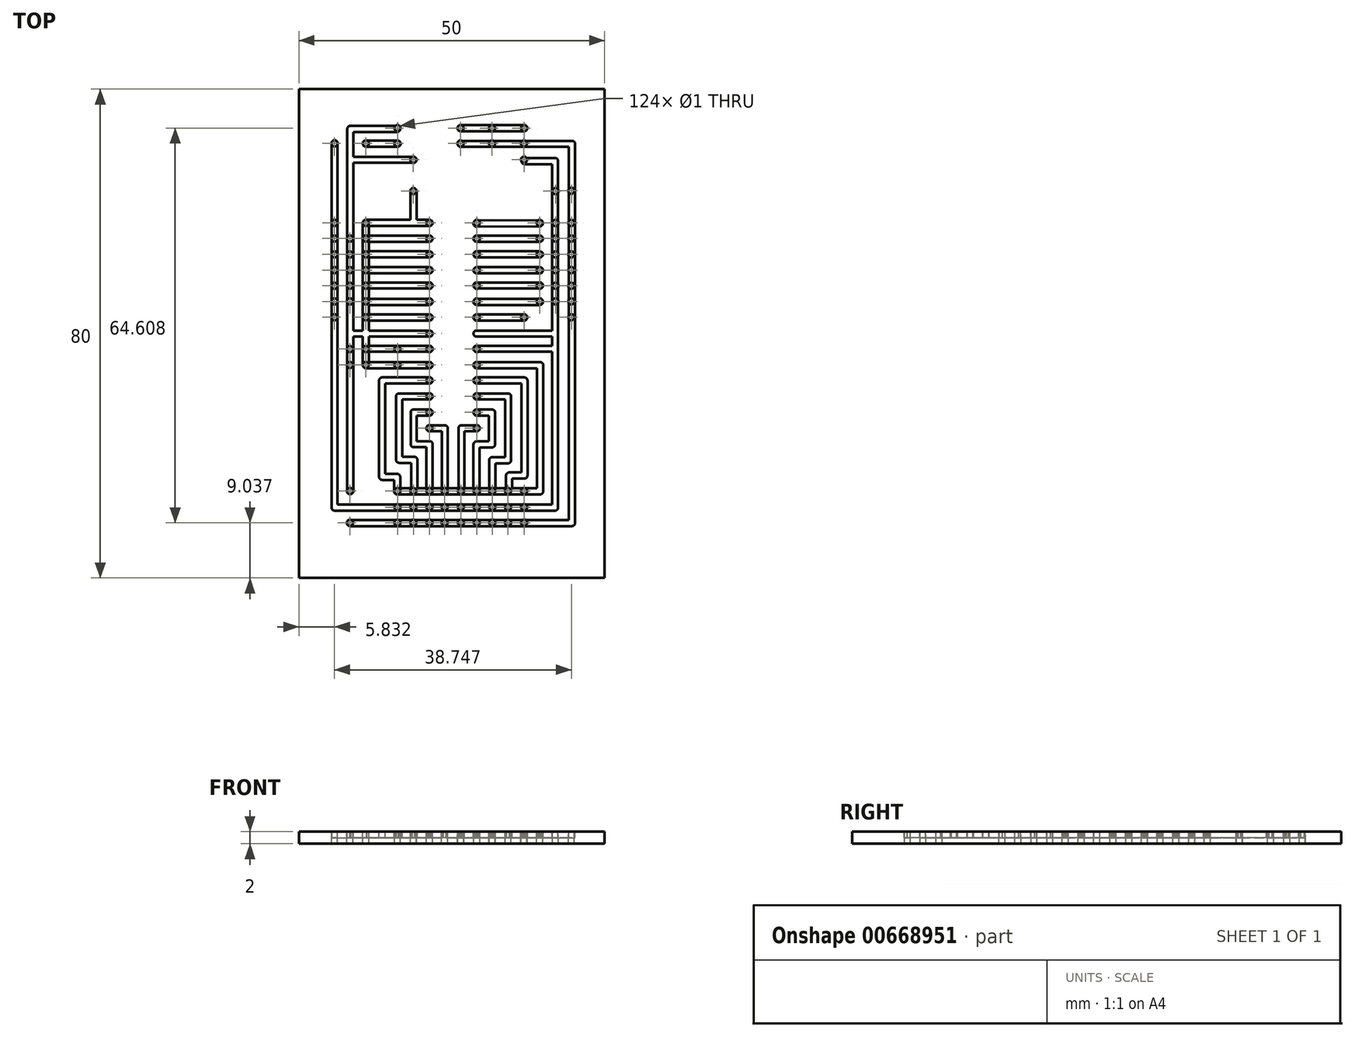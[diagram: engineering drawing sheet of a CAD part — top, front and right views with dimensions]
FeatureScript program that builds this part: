
annotation { "Feature Type Name" : "Feature", "Feature Type Description" : "" }
export const myFeature = defineFeature(function(context is Context, id is Id, definition is map)
    precondition{}
    {
        {
            var Q0;
            Q0=qCreatedBy(makeId("Top.planeOp"),FACE);
            var sketch = newSketch(context, id + "F0", { "sketchPlane" : qUnion([Q0])});
            skLineSegment(sketch, "E0.bottom", {"start": v(-25, 40) * mm, "end": v(25, 40) * mm});
            skLineSegment(sketch, "E0.top", {"start": v(-25, -40) * mm, "end": v(25, -40) * mm});
            skLineSegment(sketch, "E0.left", {"start": v(-25, 40) * mm, "end": v(-25, -40) * mm});
            skLineSegment(sketch, "E0.right", {"start": v(25, 40) * mm, "end": v(25, -40) * mm});
            skPoint(sketch, "E0.middle", {"position": v(0, 0) * mm});
            skPoint(sketch, "E1", {"position": v(0, 40) * mm});
            skLineSegment(sketch, "E2", {"start": v(0, 40) * mm, "end": v(0, 33.96) * mm});
            skPoint(sketch, "E3", {"position": v(-49.19, 30.9) * mm});
            skLineSegment(sketch, "E4", {"start": v(-19.68, -34.25) * mm, "end": v(20.32, -34.25) * mm});
            skSolve(sketch);
        }
        {
            var Q0;
            Q0=makeQuery(id+"F0.imprint","IMPRINT",FACE,{"disambiguationData":[TD([[makeQuery(id+"F0.imprint","IMPRINT",EDGE,{"derivedFrom":sQuery(id+"F0.wireOp",EDGE,"E0.top")}),1.0]])]});
            var sketch = newSketch(context, id + "F1", { "sketchPlane" : qUnion([Q0])});
            skLineSegment(sketch, "E5", {"start": v(-19.15, 31.14) * mm, "end": v(-19.15, -28.48) * mm});
            skLineSegment(sketch, "E6", {"start": v(-19.15, -28.48) * mm, "end": v(16.9, -28.48) * mm});
            skLineSegment(sketch, "E7", {"start": v(16.9, -28.48) * mm, "end": v(16.9, 28.23) * mm});
            skLineSegment(sketch, "E8", {"start": v(16.9, 28.23) * mm, "end": v(11.93, 28.23) * mm});
            skLineSegment(sketch, "E9", {"start": v(4.07, 5.19) * mm, "end": v(14.43, 5.19) * mm});
            skLineSegment(sketch, "E10", {"start": v(4.07, 7.87) * mm, "end": v(14.43, 7.87) * mm});
            skLineSegment(sketch, "E11", {"start": v(4.07, 10.35) * mm, "end": v(14.43, 10.35) * mm});
            skLineSegment(sketch, "E12", {"start": v(4.07, 12.96) * mm, "end": v(14.43, 12.96) * mm});
            skLineSegment(sketch, "E13", {"start": v(4.07, 15.53) * mm, "end": v(14.43, 15.53) * mm});
            skLineSegment(sketch, "E14", {"start": v(4.07, 17.98) * mm, "end": v(14.43, 18.06) * mm});
            skLineSegment(sketch, "E15", {"start": v(4.07, 2.63) * mm, "end": v(11.86, 2.63) * mm});
            skLineSegment(sketch, "E16", {"start": v(4.07, 0) * mm, "end": v(16.9, 0) * mm});
            skLineSegment(sketch, "E17", {"start": v(4.07, -2.48) * mm, "end": v(16.9, -2.48) * mm});
            skLineSegment(sketch, "E18", {"start": v(4.07, -5.17) * mm, "end": v(14.47, -5.17) * mm});
            skLineSegment(sketch, "E19", {"start": v(14.47, -5.17) * mm, "end": v(14.47, -25.82) * mm});
            skLineSegment(sketch, "E20", {"start": v(14.47, -25.82) * mm, "end": v(11.84, -25.82) * mm});
            skLineSegment(sketch, "E21", {"start": v(11.84, -25.82) * mm, "end": v(-8.92, -25.82) * mm});
            skLineSegment(sketch, "E22", {"start": v(-8.92, -25.82) * mm, "end": v(-8.92, -23.45) * mm});
            skLineSegment(sketch, "E23", {"start": v(-8.92, -23.45) * mm, "end": v(-11.37, -23.45) * mm});
            skLineSegment(sketch, "E24", {"start": v(-11.37, -23.45) * mm, "end": v(-11.37, -7.68) * mm});
            skLineSegment(sketch, "E25", {"start": v(-11.37, -7.68) * mm, "end": v(-3.63, -7.68) * mm});
            skLineSegment(sketch, "E26", {"start": v(-3.63, 18.1) * mm, "end": v(-14.04, 18.1) * mm});
            skLineSegment(sketch, "E27", {"start": v(-14.04, 18.1) * mm, "end": v(-14.04, -5.18) * mm});
            skLineSegment(sketch, "E28", {"start": v(-3.63, 15.53) * mm, "end": v(-14.04, 15.53) * mm});
            skLineSegment(sketch, "E29", {"start": v(-3.63, 12.96) * mm, "end": v(-14.04, 12.96) * mm});
            skLineSegment(sketch, "E30", {"start": v(-3.63, 10.35) * mm, "end": v(-14.04, 10.35) * mm});
            skLineSegment(sketch, "E31", {"start": v(-3.63, 7.87) * mm, "end": v(-14.04, 7.87) * mm});
            skLineSegment(sketch, "E32", {"start": v(-3.63, 5.19) * mm, "end": v(-14.04, 5.19) * mm});
            skLineSegment(sketch, "E33", {"start": v(-3.63, 2.63) * mm, "end": v(-14.04, 2.63) * mm});
            skLineSegment(sketch, "E34", {"start": v(-3.63, -2.48) * mm, "end": v(-14.04, -2.48) * mm});
            skLineSegment(sketch, "E35", {"start": v(-3.63, -5.17) * mm, "end": v(-14.04, -5.18) * mm});
            skLineSegment(sketch, "E36", {"start": v(4.07, -7.68) * mm, "end": v(11.9, -7.68) * mm});
            skLineSegment(sketch, "E37", {"start": v(11.9, -7.68) * mm, "end": v(11.9, -23.23) * mm});
            skLineSegment(sketch, "E38", {"start": v(11.9, -23.23) * mm, "end": v(9.4, -23.23) * mm});
            skLineSegment(sketch, "E39", {"start": v(9.4, -23.23) * mm, "end": v(9.4, -25.82) * mm});
            skLineSegment(sketch, "E40", {"start": v(4.07, -10.3) * mm, "end": v(9.22, -10.3) * mm});
            skLineSegment(sketch, "E41", {"start": v(9.22, -10.3) * mm, "end": v(9.22, -20.73) * mm});
            skLineSegment(sketch, "E42", {"start": v(9.22, -20.73) * mm, "end": v(6.63, -20.73) * mm});
            skLineSegment(sketch, "E43", {"start": v(6.63, -20.73) * mm, "end": v(6.63, -25.82) * mm});
            skLineSegment(sketch, "E44", {"start": v(4.07, -12.92) * mm, "end": v(6.59, -12.92) * mm});
            skLineSegment(sketch, "E45", {"start": v(6.59, -12.92) * mm, "end": v(6.59, -18.14) * mm});
            skLineSegment(sketch, "E46", {"start": v(6.59, -18.14) * mm, "end": v(4.07, -18.14) * mm});
            skLineSegment(sketch, "E47", {"start": v(4.07, -18.14) * mm, "end": v(4.07, -25.82) * mm});
            skLineSegment(sketch, "E48", {"start": v(1.6, -15.5) * mm, "end": v(1.6, -25.82) * mm});
            skLineSegment(sketch, "E49", {"start": v(-1.13, -25.82) * mm, "end": v(-1.13, -15.5) * mm});
            skLineSegment(sketch, "E50", {"start": v(-3.63, -25.82) * mm, "end": v(-3.63, -18.1) * mm});
            skLineSegment(sketch, "E51", {"start": v(-3.63, -18.1) * mm, "end": v(-6.21, -18.1) * mm});
            skLineSegment(sketch, "E52", {"start": v(-3.63, -10.3) * mm, "end": v(-8.6, -10.3) * mm});
            skLineSegment(sketch, "E53", {"start": v(-8.6, -10.3) * mm, "end": v(-8.6, -20.65) * mm});
            skLineSegment(sketch, "E54", {"start": v(-8.6, -20.65) * mm, "end": v(-6.11, -20.65) * mm});
            skLineSegment(sketch, "E55", {"start": v(-6.11, -20.65) * mm, "end": v(-6.11, -25.82) * mm});
            skLineSegment(sketch, "E56", {"start": v(-3.63, -12.92) * mm, "end": v(-6.21, -12.92) * mm});
            skLineSegment(sketch, "E57", {"start": v(-6.21, -12.92) * mm, "end": v(-6.21, -18.1) * mm});
            skLineSegment(sketch, "E58", {"start": v(-6.25, 23.32) * mm, "end": v(-6.25, 18.1) * mm});
            skLineSegment(sketch, "E59", {"start": v(-3.63, 0) * mm, "end": v(-16.57, 0) * mm});
            skLineSegment(sketch, "E60", {"start": v(-16.57, 0) * mm, "end": v(-16.57, 33.5) * mm});
            skLineSegment(sketch, "E61", {"start": v(-16.57, 33.5) * mm, "end": v(-8.92, 33.5) * mm});
            skLineSegment(sketch, "E62", {"start": v(-14.04, 31.08) * mm, "end": v(-8.84, 31.08) * mm});
            skLineSegment(sketch, "E63", {"start": v(-6.24, 28.44) * mm, "end": v(-16.57, 28.44) * mm});
            skLineSegment(sketch, "E64", {"start": v(1.48, 33.63) * mm, "end": v(11.88, 33.63) * mm});
            skLineSegment(sketch, "E65", {"start": v(1.48, 31.05) * mm, "end": v(19.67, 31.05) * mm});
            skLineSegment(sketch, "E66", {"start": v(19.67, 31.05) * mm, "end": v(19.67, -31) * mm});
            skLineSegment(sketch, "E67", {"start": v(19.67, -31) * mm, "end": v(-16.64, -31) * mm});
            skLineSegment(sketch, "E68", {"start": v(-16.57, 0) * mm, "end": v(-16.57, -25.78) * mm});
            skLineSegment(sketch, "E69", {"start": v(-3.64, -15.5) * mm, "end": v(-1.13, -15.5) * mm});
            skLineSegment(sketch, "E70", {"start": v(1.6, -15.5) * mm, "end": v(4.07, -15.5) * mm});
            skArc(sketch, "E71.0.startCap", {"start": v(-3.63, 16.03) * mm, "mid": v(-3.13, 15.53) * mm, "end": v(-3.63, 15.03) * mm});
            skArc(sketch, "E71.0.endCap", {"start": v(-14.04, 15.03) * mm, "mid": v(-14.54, 15.53) * mm, "end": v(-14.04, 16.03) * mm});
            skLineSegment(sketch, "E71.0.left", {"start": v(-3.63, 15.03) * mm, "end": v(-14.04, 15.03) * mm});
            skLineSegment(sketch, "E71.0.right", {"start": v(-3.63, 16.03) * mm, "end": v(-14.04, 16.03) * mm});
            skArc(sketch, "E71.1.startCap", {"start": v(11.4, -7.68) * mm, "mid": v(11.9, -7.18) * mm, "end": v(12.4, -7.68) * mm});
            skArc(sketch, "E71.1.endCap", {"start": v(12.4, -23.23) * mm, "mid": v(11.9, -23.73) * mm, "end": v(11.4, -23.23) * mm});
            skLineSegment(sketch, "E71.1.left", {"start": v(12.4, -7.68) * mm, "end": v(12.4, -23.23) * mm});
            skLineSegment(sketch, "E71.1.right", {"start": v(11.4, -7.68) * mm, "end": v(11.4, -23.23) * mm});
            skArc(sketch, "E71.2.endCap", {"start": v(-16.07, -25.78) * mm, "mid": v(-16.57, -26.28) * mm, "end": v(-17.07, -25.78) * mm});
            skLineSegment(sketch, "E71.2.left", {"start": v(-16.07, 0) * mm, "end": v(-16.07, -25.78) * mm});
            skLineSegment(sketch, "E71.2.right", {"start": v(-17.07, 0) * mm, "end": v(-17.07, -25.78) * mm});
            skArc(sketch, "E71.3.startCap", {"start": v(4.07, 7.37) * mm, "mid": v(3.57, 7.87) * mm, "end": v(4.07, 8.37) * mm});
            skArc(sketch, "E71.3.endCap", {"start": v(14.43, 8.37) * mm, "mid": v(14.93, 7.87) * mm, "end": v(14.43, 7.37) * mm});
            skLineSegment(sketch, "E71.3.left", {"start": v(4.07, 8.37) * mm, "end": v(14.43, 8.37) * mm});
            skLineSegment(sketch, "E71.3.right", {"start": v(4.07, 7.37) * mm, "end": v(14.43, 7.37) * mm});
            skArc(sketch, "E71.4.startCap", {"start": v(-8.92, -22.95) * mm, "mid": v(-8.42, -23.45) * mm, "end": v(-8.92, -23.95) * mm});
            skArc(sketch, "E71.4.endCap", {"start": v(-11.37, -23.95) * mm, "mid": v(-11.87, -23.45) * mm, "end": v(-11.37, -22.95) * mm});
            skLineSegment(sketch, "E71.4.left", {"start": v(-8.92, -23.95) * mm, "end": v(-11.37, -23.95) * mm});
            skLineSegment(sketch, "E71.4.right", {"start": v(-8.92, -22.95) * mm, "end": v(-11.37, -22.95) * mm});
            skArc(sketch, "E71.5.startCap", {"start": v(11.84, -25.32) * mm, "mid": v(12.34, -25.82) * mm, "end": v(11.84, -26.32) * mm});
            skArc(sketch, "E71.5.endCap", {"start": v(-8.92, -26.32) * mm, "mid": v(-9.42, -25.82) * mm, "end": v(-8.92, -25.32) * mm});
            skLineSegment(sketch, "E71.5.left", {"start": v(11.84, -26.32) * mm, "end": v(-8.92, -26.32) * mm});
            skLineSegment(sketch, "E71.5.right", {"start": v(11.84, -25.32) * mm, "end": v(-8.92, -25.32) * mm});
            skArc(sketch, "E71.6.startCap", {"start": v(11.9, -22.73) * mm, "mid": v(12.4, -23.23) * mm, "end": v(11.9, -23.73) * mm});
            skArc(sketch, "E71.6.endCap", {"start": v(9.4, -23.73) * mm, "mid": v(8.9, -23.23) * mm, "end": v(9.4, -22.73) * mm});
            skLineSegment(sketch, "E71.6.left", {"start": v(11.9, -23.73) * mm, "end": v(9.4, -23.73) * mm});
            skLineSegment(sketch, "E71.6.right", {"start": v(11.9, -22.73) * mm, "end": v(9.4, -22.73) * mm});
            skArc(sketch, "E71.7.startCap", {"start": v(-8.6, -21.15) * mm, "mid": v(-9.1, -20.65) * mm, "end": v(-8.6, -20.15) * mm});
            skArc(sketch, "E71.7.endCap", {"start": v(-6.11, -20.15) * mm, "mid": v(-5.61, -20.65) * mm, "end": v(-6.11, -21.15) * mm});
            skLineSegment(sketch, "E71.7.left", {"start": v(-8.6, -20.15) * mm, "end": v(-6.11, -20.15) * mm});
            skLineSegment(sketch, "E71.7.right", {"start": v(-8.6, -21.15) * mm, "end": v(-6.11, -21.15) * mm});
            skArc(sketch, "E71.8.startCap", {"start": v(19.67, -30.5) * mm, "mid": v(20.17, -31) * mm, "end": v(19.67, -31.5) * mm});
            skArc(sketch, "E71.8.endCap", {"start": v(-16.64, -31.5) * mm, "mid": v(-17.14, -31) * mm, "end": v(-16.64, -30.5) * mm});
            skLineSegment(sketch, "E71.8.left", {"start": v(19.67, -31.5) * mm, "end": v(-16.64, -31.5) * mm});
            skLineSegment(sketch, "E71.8.right", {"start": v(19.67, -30.5) * mm, "end": v(-16.64, -30.5) * mm});
            skArc(sketch, "E71.9.startCap", {"start": v(-3.64, -16) * mm, "mid": v(-4.14, -15.5) * mm, "end": v(-3.64, -15) * mm});
            skArc(sketch, "E71.9.endCap", {"start": v(-1.13, -15) * mm, "mid": v(-0.63, -15.5) * mm, "end": v(-1.13, -16) * mm});
            skLineSegment(sketch, "E71.9.left", {"start": v(-3.64, -15) * mm, "end": v(-1.13, -15) * mm});
            skLineSegment(sketch, "E71.9.right", {"start": v(-3.64, -16) * mm, "end": v(-1.13, -16) * mm});
            skArc(sketch, "E71.10.startCap", {"start": v(6.13, -20.73) * mm, "mid": v(6.63, -20.23) * mm, "end": v(7.13, -20.73) * mm});
            skArc(sketch, "E71.10.endCap", {"start": v(7.13, -25.82) * mm, "mid": v(6.63, -26.32) * mm, "end": v(6.13, -25.82) * mm});
            skLineSegment(sketch, "E71.10.left", {"start": v(7.13, -20.73) * mm, "end": v(7.13, -25.82) * mm});
            skLineSegment(sketch, "E71.10.right", {"start": v(6.13, -20.73) * mm, "end": v(6.13, -25.82) * mm});
            skArc(sketch, "E71.11.startCap", {"start": v(14.47, -25.32) * mm, "mid": v(14.97, -25.82) * mm, "end": v(14.47, -26.32) * mm});
            skArc(sketch, "E71.11.endCap", {"start": v(11.84, -26.32) * mm, "mid": v(11.34, -25.82) * mm, "end": v(11.84, -25.32) * mm});
            skLineSegment(sketch, "E71.11.left", {"start": v(14.47, -26.32) * mm, "end": v(11.84, -26.32) * mm});
            skLineSegment(sketch, "E71.11.right", {"start": v(14.47, -25.32) * mm, "end": v(11.84, -25.32) * mm});
            skArc(sketch, "E71.12.startCap", {"start": v(4.07, -8.18) * mm, "mid": v(3.57, -7.68) * mm, "end": v(4.07, -7.18) * mm});
            skArc(sketch, "E71.12.endCap", {"start": v(11.9, -7.18) * mm, "mid": v(12.4, -7.68) * mm, "end": v(11.9, -8.18) * mm});
            skLineSegment(sketch, "E71.12.left", {"start": v(4.07, -7.18) * mm, "end": v(11.9, -7.18) * mm});
            skLineSegment(sketch, "E71.12.right", {"start": v(4.07, -8.18) * mm, "end": v(11.9, -8.18) * mm});
            skArc(sketch, "E71.13.startCap", {"start": v(4.07, 2.13) * mm, "mid": v(3.57, 2.63) * mm, "end": v(4.07, 3.13) * mm});
            skArc(sketch, "E71.13.endCap", {"start": v(11.86, 3.13) * mm, "mid": v(12.36, 2.63) * mm, "end": v(11.86, 2.13) * mm});
            skLineSegment(sketch, "E71.13.left", {"start": v(4.07, 3.13) * mm, "end": v(11.86, 3.13) * mm});
            skLineSegment(sketch, "E71.13.right", {"start": v(4.07, 2.13) * mm, "end": v(11.86, 2.13) * mm});
            skArc(sketch, "E71.14.startCap", {"start": v(-14.54, 18.1) * mm, "mid": v(-14.04, 18.6) * mm, "end": v(-13.54, 18.1) * mm});
            skArc(sketch, "E71.14.endCap", {"start": v(-13.54, -5.18) * mm, "mid": v(-14.04, -5.68) * mm, "end": v(-14.54, -5.18) * mm});
            skLineSegment(sketch, "E71.14.left", {"start": v(-13.54, 18.1) * mm, "end": v(-13.54, -5.18) * mm});
            skLineSegment(sketch, "E71.14.right", {"start": v(-14.54, 18.1) * mm, "end": v(-14.54, -5.18) * mm});
            skArc(sketch, "E71.15.startCap", {"start": v(-3.63, 0.5) * mm, "mid": v(-3.13, 0) * mm, "end": v(-3.63, -0.5) * mm});
            skArc(sketch, "E71.15.endCap", {"start": v(-16.57, -0.5) * mm, "mid": v(-17.07, 0) * mm, "end": v(-16.57, 0.5) * mm});
            skLineSegment(sketch, "E71.15.left", {"start": v(-3.63, -0.5) * mm, "end": v(-16.57, -0.5) * mm});
            skLineSegment(sketch, "E71.15.right", {"start": v(-3.63, 0.5) * mm, "end": v(-16.57, 0.5) * mm});
            skArc(sketch, "E71.16.startCap", {"start": v(-3.63, -9.8) * mm, "mid": v(-3.13, -10.3) * mm, "end": v(-3.63, -10.8) * mm});
            skArc(sketch, "E71.16.endCap", {"start": v(-8.6, -10.8) * mm, "mid": v(-9.1, -10.3) * mm, "end": v(-8.6, -9.8) * mm});
            skLineSegment(sketch, "E71.16.left", {"start": v(-3.63, -10.8) * mm, "end": v(-8.6, -10.8) * mm});
            skLineSegment(sketch, "E71.16.right", {"start": v(-3.63, -9.8) * mm, "end": v(-8.6, -9.8) * mm});
            skArc(sketch, "E71.17.startCap", {"start": v(4.07, -0.5) * mm, "mid": v(3.57, 0) * mm, "end": v(4.07, 0.5) * mm});
            skArc(sketch, "E71.17.endCap", {"start": v(16.9, 0.5) * mm, "mid": v(17.4, 0) * mm, "end": v(16.9, -0.5) * mm});
            skLineSegment(sketch, "E71.17.left", {"start": v(4.07, 0.5) * mm, "end": v(16.9, 0.5) * mm});
            skLineSegment(sketch, "E71.17.right", {"start": v(4.07, -0.5) * mm, "end": v(16.9, -0.5) * mm});
            skArc(sketch, "E71.18.startCap", {"start": v(4.07, -2.98) * mm, "mid": v(3.57, -2.48) * mm, "end": v(4.07, -1.98) * mm});
            skArc(sketch, "E71.18.endCap", {"start": v(16.9, -1.98) * mm, "mid": v(17.4, -2.48) * mm, "end": v(16.9, -2.98) * mm});
            skLineSegment(sketch, "E71.18.left", {"start": v(4.07, -1.98) * mm, "end": v(16.9, -1.98) * mm});
            skLineSegment(sketch, "E71.18.right", {"start": v(4.07, -2.98) * mm, "end": v(16.9, -2.98) * mm});
            skArc(sketch, "E71.19.startCap", {"start": v(-8.42, -25.82) * mm, "mid": v(-8.92, -26.32) * mm, "end": v(-9.42, -25.82) * mm});
            skArc(sketch, "E71.19.endCap", {"start": v(-9.42, -23.45) * mm, "mid": v(-8.92, -22.95) * mm, "end": v(-8.42, -23.45) * mm});
            skLineSegment(sketch, "E71.19.left", {"start": v(-9.42, -25.82) * mm, "end": v(-9.42, -23.45) * mm});
            skLineSegment(sketch, "E71.19.right", {"start": v(-8.42, -25.82) * mm, "end": v(-8.42, -23.45) * mm});
            skArc(sketch, "E71.20.startCap", {"start": v(4.07, 9.85) * mm, "mid": v(3.57, 10.35) * mm, "end": v(4.07, 10.85) * mm});
            skArc(sketch, "E71.20.endCap", {"start": v(14.43, 10.85) * mm, "mid": v(14.93, 10.35) * mm, "end": v(14.43, 9.85) * mm});
            skLineSegment(sketch, "E71.20.left", {"start": v(4.07, 10.85) * mm, "end": v(14.43, 10.85) * mm});
            skLineSegment(sketch, "E71.20.right", {"start": v(4.07, 9.85) * mm, "end": v(14.43, 9.85) * mm});
            skArc(sketch, "E71.21.startCap", {"start": v(1.6, -16) * mm, "mid": v(1.1, -15.5) * mm, "end": v(1.6, -15) * mm});
            skArc(sketch, "E71.21.endCap", {"start": v(4.07, -15) * mm, "mid": v(4.57, -15.5) * mm, "end": v(4.07, -16) * mm});
            skLineSegment(sketch, "E71.21.left", {"start": v(1.6, -15) * mm, "end": v(4.07, -15) * mm});
            skLineSegment(sketch, "E71.21.right", {"start": v(1.6, -16) * mm, "end": v(4.07, -16) * mm});
            skArc(sketch, "E71.22.startCap", {"start": v(4.07, 12.46) * mm, "mid": v(3.57, 12.96) * mm, "end": v(4.07, 13.46) * mm});
            skArc(sketch, "E71.22.endCap", {"start": v(14.43, 13.46) * mm, "mid": v(14.93, 12.96) * mm, "end": v(14.43, 12.46) * mm});
            skLineSegment(sketch, "E71.22.left", {"start": v(4.07, 13.46) * mm, "end": v(14.43, 13.46) * mm});
            skLineSegment(sketch, "E71.22.right", {"start": v(4.07, 12.46) * mm, "end": v(14.43, 12.46) * mm});
            skArc(sketch, "E71.23.startCap", {"start": v(-6.75, 23.32) * mm, "mid": v(-6.25, 23.82) * mm, "end": v(-5.75, 23.32) * mm});
            skArc(sketch, "E71.23.endCap", {"start": v(-5.75, 18.1) * mm, "mid": v(-6.25, 17.6) * mm, "end": v(-6.75, 18.1) * mm});
            skLineSegment(sketch, "E71.23.left", {"start": v(-5.75, 23.32) * mm, "end": v(-5.75, 18.1) * mm});
            skLineSegment(sketch, "E71.23.right", {"start": v(-6.75, 23.32) * mm, "end": v(-6.75, 18.1) * mm});
            skArc(sketch, "E71.24.startCap", {"start": v(-3.63, 18.6) * mm, "mid": v(-3.13, 18.1) * mm, "end": v(-3.63, 17.6) * mm});
            skArc(sketch, "E71.24.endCap", {"start": v(-14.04, 17.6) * mm, "mid": v(-14.54, 18.1) * mm, "end": v(-14.04, 18.6) * mm});
            skLineSegment(sketch, "E71.24.left", {"start": v(-3.63, 17.6) * mm, "end": v(-14.04, 17.6) * mm});
            skLineSegment(sketch, "E71.24.right", {"start": v(-3.63, 18.6) * mm, "end": v(-14.04, 18.6) * mm});
            skArc(sketch, "E71.25.startCap", {"start": v(-19.65, 31.14) * mm, "mid": v(-19.15, 31.64) * mm, "end": v(-18.65, 31.14) * mm});
            skArc(sketch, "E71.25.endCap", {"start": v(-18.65, -28.48) * mm, "mid": v(-19.15, -28.98) * mm, "end": v(-19.65, -28.48) * mm});
            skLineSegment(sketch, "E71.25.left", {"start": v(-18.65, 31.14) * mm, "end": v(-18.65, -28.48) * mm});
            skLineSegment(sketch, "E71.25.right", {"start": v(-19.65, 31.14) * mm, "end": v(-19.65, -28.48) * mm});
            skArc(sketch, "E71.26.startCap", {"start": v(1.1, -15.5) * mm, "mid": v(1.6, -15) * mm, "end": v(2.1, -15.5) * mm});
            skArc(sketch, "E71.26.endCap", {"start": v(2.1, -25.82) * mm, "mid": v(1.6, -26.32) * mm, "end": v(1.1, -25.82) * mm});
            skLineSegment(sketch, "E71.26.left", {"start": v(2.1, -15.5) * mm, "end": v(2.1, -25.82) * mm});
            skLineSegment(sketch, "E71.26.right", {"start": v(1.1, -15.5) * mm, "end": v(1.1, -25.82) * mm});
            skArc(sketch, "E71.27.startCap", {"start": v(-3.63, 5.69) * mm, "mid": v(-3.13, 5.19) * mm, "end": v(-3.63, 4.69) * mm});
            skArc(sketch, "E71.27.endCap", {"start": v(-14.04, 4.69) * mm, "mid": v(-14.54, 5.19) * mm, "end": v(-14.04, 5.69) * mm});
            skLineSegment(sketch, "E71.27.left", {"start": v(-3.63, 4.69) * mm, "end": v(-14.04, 4.69) * mm});
            skLineSegment(sketch, "E71.27.right", {"start": v(-3.63, 5.69) * mm, "end": v(-14.04, 5.69) * mm});
            skArc(sketch, "E71.28.startCap", {"start": v(4.07, 17.48) * mm, "mid": v(3.57, 17.98) * mm, "end": v(4.06, 18.48) * mm});
            skArc(sketch, "E71.28.endCap", {"start": v(14.42, 18.56) * mm, "mid": v(14.93, 18.06) * mm, "end": v(14.43, 17.56) * mm});
            skLineSegment(sketch, "E71.28.left", {"start": v(4.06, 18.48) * mm, "end": v(14.42, 18.56) * mm});
            skLineSegment(sketch, "E71.28.right", {"start": v(4.07, 17.48) * mm, "end": v(14.43, 17.56) * mm});
            skArc(sketch, "E71.29.startCap", {"start": v(4.07, 15.03) * mm, "mid": v(3.57, 15.53) * mm, "end": v(4.07, 16.03) * mm});
            skArc(sketch, "E71.29.endCap", {"start": v(14.43, 16.03) * mm, "mid": v(14.93, 15.53) * mm, "end": v(14.43, 15.03) * mm});
            skLineSegment(sketch, "E71.29.left", {"start": v(4.07, 16.03) * mm, "end": v(14.43, 16.03) * mm});
            skLineSegment(sketch, "E71.29.right", {"start": v(4.07, 15.03) * mm, "end": v(14.43, 15.03) * mm});
            skArc(sketch, "E71.30.startCap", {"start": v(-6.61, -20.65) * mm, "mid": v(-6.11, -20.15) * mm, "end": v(-5.61, -20.65) * mm});
            skArc(sketch, "E71.30.endCap", {"start": v(-5.61, -25.82) * mm, "mid": v(-6.11, -26.32) * mm, "end": v(-6.61, -25.82) * mm});
            skLineSegment(sketch, "E71.30.left", {"start": v(-5.61, -20.65) * mm, "end": v(-5.61, -25.82) * mm});
            skLineSegment(sketch, "E71.30.right", {"start": v(-6.61, -20.65) * mm, "end": v(-6.61, -25.82) * mm});
            skArc(sketch, "E71.31.startCap", {"start": v(1.48, 30.55) * mm, "mid": v(0.98, 31.05) * mm, "end": v(1.48, 31.55) * mm});
            skArc(sketch, "E71.31.endCap", {"start": v(19.67, 31.55) * mm, "mid": v(20.17, 31.05) * mm, "end": v(19.67, 30.55) * mm});
            skLineSegment(sketch, "E71.31.left", {"start": v(1.48, 31.55) * mm, "end": v(19.67, 31.55) * mm});
            skLineSegment(sketch, "E71.31.right", {"start": v(1.48, 30.55) * mm, "end": v(19.67, 30.55) * mm});
            skArc(sketch, "E71.32.startCap", {"start": v(-6.71, -12.92) * mm, "mid": v(-6.21, -12.42) * mm, "end": v(-5.71, -12.92) * mm});
            skArc(sketch, "E71.32.endCap", {"start": v(-5.71, -18.1) * mm, "mid": v(-6.21, -18.6) * mm, "end": v(-6.71, -18.1) * mm});
            skLineSegment(sketch, "E71.32.left", {"start": v(-5.71, -12.92) * mm, "end": v(-5.71, -18.1) * mm});
            skLineSegment(sketch, "E71.32.right", {"start": v(-6.71, -12.92) * mm, "end": v(-6.71, -18.1) * mm});
            skArc(sketch, "E71.33.startCap", {"start": v(-11.37, -8.18) * mm, "mid": v(-11.87, -7.68) * mm, "end": v(-11.37, -7.18) * mm});
            skArc(sketch, "E71.33.endCap", {"start": v(-3.63, -7.18) * mm, "mid": v(-3.13, -7.68) * mm, "end": v(-3.63, -8.18) * mm});
            skLineSegment(sketch, "E71.33.left", {"start": v(-11.37, -7.18) * mm, "end": v(-3.63, -7.18) * mm});
            skLineSegment(sketch, "E71.33.right", {"start": v(-11.37, -8.18) * mm, "end": v(-3.63, -8.18) * mm});
            skArc(sketch, "E71.34.startCap", {"start": v(17.4, -28.48) * mm, "mid": v(16.9, -28.98) * mm, "end": v(16.4, -28.48) * mm});
            skArc(sketch, "E71.34.endCap", {"start": v(16.4, 28.23) * mm, "mid": v(16.9, 28.73) * mm, "end": v(17.4, 28.23) * mm});
            skLineSegment(sketch, "E71.34.left", {"start": v(16.4, -28.48) * mm, "end": v(16.4, 28.23) * mm});
            skLineSegment(sketch, "E71.34.right", {"start": v(17.4, -28.48) * mm, "end": v(17.4, 28.23) * mm});
            skArc(sketch, "E71.35.startCap", {"start": v(-3.63, 3.13) * mm, "mid": v(-3.13, 2.63) * mm, "end": v(-3.63, 2.13) * mm});
            skArc(sketch, "E71.35.endCap", {"start": v(-14.04, 2.13) * mm, "mid": v(-14.54, 2.63) * mm, "end": v(-14.04, 3.13) * mm});
            skLineSegment(sketch, "E71.35.left", {"start": v(-3.63, 2.13) * mm, "end": v(-14.04, 2.13) * mm});
            skLineSegment(sketch, "E71.35.right", {"start": v(-3.63, 3.13) * mm, "end": v(-14.04, 3.13) * mm});
            skArc(sketch, "E71.36.startCap", {"start": v(-16.57, 33) * mm, "mid": v(-17.07, 33.5) * mm, "end": v(-16.57, 34) * mm});
            skArc(sketch, "E71.36.endCap", {"start": v(-8.92, 34) * mm, "mid": v(-8.42, 33.5) * mm, "end": v(-8.92, 33) * mm});
            skLineSegment(sketch, "E71.36.left", {"start": v(-16.57, 34) * mm, "end": v(-8.92, 34) * mm});
            skLineSegment(sketch, "E71.36.right", {"start": v(-16.57, 33) * mm, "end": v(-8.92, 33) * mm});
            skArc(sketch, "E71.37.startCap", {"start": v(6.09, -12.92) * mm, "mid": v(6.59, -12.42) * mm, "end": v(7.09, -12.92) * mm});
            skArc(sketch, "E71.37.endCap", {"start": v(7.09, -18.14) * mm, "mid": v(6.59, -18.64) * mm, "end": v(6.09, -18.14) * mm});
            skLineSegment(sketch, "E71.37.left", {"start": v(7.09, -12.92) * mm, "end": v(7.09, -18.14) * mm});
            skLineSegment(sketch, "E71.37.right", {"start": v(6.09, -12.92) * mm, "end": v(6.09, -18.14) * mm});
            skArc(sketch, "E71.38.startCap", {"start": v(-9.1, -10.3) * mm, "mid": v(-8.6, -9.8) * mm, "end": v(-8.1, -10.3) * mm});
            skArc(sketch, "E71.38.endCap", {"start": v(-8.1, -20.65) * mm, "mid": v(-8.6, -21.15) * mm, "end": v(-9.1, -20.65) * mm});
            skLineSegment(sketch, "E71.38.left", {"start": v(-8.1, -10.3) * mm, "end": v(-8.1, -20.65) * mm});
            skLineSegment(sketch, "E71.38.right", {"start": v(-9.1, -10.3) * mm, "end": v(-9.1, -20.65) * mm});
            skArc(sketch, "E71.39.startCap", {"start": v(-3.63, 13.46) * mm, "mid": v(-3.13, 12.96) * mm, "end": v(-3.63, 12.46) * mm});
            skArc(sketch, "E71.39.endCap", {"start": v(-14.04, 12.46) * mm, "mid": v(-14.54, 12.96) * mm, "end": v(-14.04, 13.46) * mm});
            skLineSegment(sketch, "E71.39.left", {"start": v(-3.63, 12.46) * mm, "end": v(-14.04, 12.46) * mm});
            skLineSegment(sketch, "E71.39.right", {"start": v(-3.63, 13.46) * mm, "end": v(-14.04, 13.46) * mm});
            skArc(sketch, "E71.40.startCap", {"start": v(4.07, 4.69) * mm, "mid": v(3.57, 5.19) * mm, "end": v(4.07, 5.69) * mm});
            skArc(sketch, "E71.40.endCap", {"start": v(14.43, 5.69) * mm, "mid": v(14.93, 5.19) * mm, "end": v(14.43, 4.69) * mm});
            skLineSegment(sketch, "E71.40.left", {"start": v(4.07, 5.69) * mm, "end": v(14.43, 5.69) * mm});
            skLineSegment(sketch, "E71.40.right", {"start": v(4.07, 4.69) * mm, "end": v(14.43, 4.69) * mm});
            skArc(sketch, "E71.41.startCap", {"start": v(16.9, 28.73) * mm, "mid": v(17.4, 28.23) * mm, "end": v(16.9, 27.73) * mm});
            skArc(sketch, "E71.41.endCap", {"start": v(11.93, 27.73) * mm, "mid": v(11.43, 28.23) * mm, "end": v(11.93, 28.73) * mm});
            skLineSegment(sketch, "E71.41.left", {"start": v(16.9, 27.73) * mm, "end": v(11.93, 27.73) * mm});
            skLineSegment(sketch, "E71.41.right", {"start": v(16.9, 28.73) * mm, "end": v(11.93, 28.73) * mm});
            skArc(sketch, "E71.42.startCap", {"start": v(-3.63, 10.85) * mm, "mid": v(-3.13, 10.35) * mm, "end": v(-3.63, 9.85) * mm});
            skArc(sketch, "E71.42.endCap", {"start": v(-14.04, 9.85) * mm, "mid": v(-14.54, 10.35) * mm, "end": v(-14.04, 10.85) * mm});
            skLineSegment(sketch, "E71.42.left", {"start": v(-3.63, 9.85) * mm, "end": v(-14.04, 9.85) * mm});
            skLineSegment(sketch, "E71.42.right", {"start": v(-3.63, 10.85) * mm, "end": v(-14.04, 10.85) * mm});
            skArc(sketch, "E71.43.startCap", {"start": v(19.17, 31.05) * mm, "mid": v(19.67, 31.55) * mm, "end": v(20.17, 31.05) * mm});
            skArc(sketch, "E71.43.endCap", {"start": v(20.17, -31) * mm, "mid": v(19.67, -31.5) * mm, "end": v(19.17, -31) * mm});
            skLineSegment(sketch, "E71.43.left", {"start": v(20.17, 31.05) * mm, "end": v(20.17, -31) * mm});
            skLineSegment(sketch, "E71.43.right", {"start": v(19.17, 31.05) * mm, "end": v(19.17, -31) * mm});
            skArc(sketch, "E71.44.startCap", {"start": v(1.48, 33.13) * mm, "mid": v(0.98, 33.63) * mm, "end": v(1.48, 34.13) * mm});
            skArc(sketch, "E71.44.endCap", {"start": v(11.88, 34.13) * mm, "mid": v(12.38, 33.63) * mm, "end": v(11.88, 33.13) * mm});
            skLineSegment(sketch, "E71.44.left", {"start": v(1.48, 34.13) * mm, "end": v(11.88, 34.13) * mm});
            skLineSegment(sketch, "E71.44.right", {"start": v(1.48, 33.13) * mm, "end": v(11.88, 33.13) * mm});
            skArc(sketch, "E71.45.startCap", {"start": v(-19.15, -28.98) * mm, "mid": v(-19.65, -28.48) * mm, "end": v(-19.15, -27.98) * mm});
            skArc(sketch, "E71.45.endCap", {"start": v(16.9, -27.98) * mm, "mid": v(17.4, -28.48) * mm, "end": v(16.9, -28.98) * mm});
            skLineSegment(sketch, "E71.45.left", {"start": v(-19.15, -27.98) * mm, "end": v(16.9, -27.98) * mm});
            skLineSegment(sketch, "E71.45.right", {"start": v(-19.15, -28.98) * mm, "end": v(16.9, -28.98) * mm});
            skArc(sketch, "E71.46.startCap", {"start": v(8.9, -23.23) * mm, "mid": v(9.4, -22.73) * mm, "end": v(9.9, -23.23) * mm});
            skArc(sketch, "E71.46.endCap", {"start": v(9.9, -25.82) * mm, "mid": v(9.4, -26.32) * mm, "end": v(8.9, -25.82) * mm});
            skLineSegment(sketch, "E71.46.left", {"start": v(9.9, -23.23) * mm, "end": v(9.9, -25.82) * mm});
            skLineSegment(sketch, "E71.46.right", {"start": v(8.9, -23.23) * mm, "end": v(8.9, -25.82) * mm});
            skArc(sketch, "E71.47.startCap", {"start": v(-3.13, -25.82) * mm, "mid": v(-3.63, -26.32) * mm, "end": v(-4.13, -25.82) * mm});
            skArc(sketch, "E71.47.endCap", {"start": v(-4.13, -18.1) * mm, "mid": v(-3.63, -17.6) * mm, "end": v(-3.13, -18.1) * mm});
            skLineSegment(sketch, "E71.47.left", {"start": v(-4.13, -25.82) * mm, "end": v(-4.13, -18.1) * mm});
            skLineSegment(sketch, "E71.47.right", {"start": v(-3.13, -25.82) * mm, "end": v(-3.13, -18.1) * mm});
            skArc(sketch, "E71.48.startCap", {"start": v(-3.63, -1.98) * mm, "mid": v(-3.13, -2.48) * mm, "end": v(-3.63, -2.98) * mm});
            skArc(sketch, "E71.48.endCap", {"start": v(-14.04, -2.98) * mm, "mid": v(-14.54, -2.48) * mm, "end": v(-14.04, -1.98) * mm});
            skLineSegment(sketch, "E71.48.left", {"start": v(-3.63, -2.98) * mm, "end": v(-14.04, -2.98) * mm});
            skLineSegment(sketch, "E71.48.right", {"start": v(-3.63, -1.98) * mm, "end": v(-14.04, -1.98) * mm});
            skArc(sketch, "E71.49.startCap", {"start": v(8.72, -10.3) * mm, "mid": v(9.22, -9.8) * mm, "end": v(9.72, -10.3) * mm});
            skArc(sketch, "E71.49.endCap", {"start": v(9.72, -20.73) * mm, "mid": v(9.22, -21.23) * mm, "end": v(8.72, -20.73) * mm});
            skLineSegment(sketch, "E71.49.left", {"start": v(9.72, -10.3) * mm, "end": v(9.72, -20.73) * mm});
            skLineSegment(sketch, "E71.49.right", {"start": v(8.72, -10.3) * mm, "end": v(8.72, -20.73) * mm});
            skArc(sketch, "E71.50.endCap", {"start": v(-17.07, 33.5) * mm, "mid": v(-16.57, 34) * mm, "end": v(-16.07, 33.5) * mm});
            skLineSegment(sketch, "E71.50.left", {"start": v(-17.07, 0) * mm, "end": v(-17.07, 33.5) * mm});
            skLineSegment(sketch, "E71.50.right", {"start": v(-16.07, 0) * mm, "end": v(-16.07, 33.5) * mm});
            skArc(sketch, "E71.51.startCap", {"start": v(4.07, -13.42) * mm, "mid": v(3.57, -12.92) * mm, "end": v(4.07, -12.42) * mm});
            skArc(sketch, "E71.51.endCap", {"start": v(6.59, -12.42) * mm, "mid": v(7.09, -12.92) * mm, "end": v(6.59, -13.42) * mm});
            skLineSegment(sketch, "E71.51.left", {"start": v(4.07, -12.42) * mm, "end": v(6.59, -12.42) * mm});
            skLineSegment(sketch, "E71.51.right", {"start": v(4.07, -13.42) * mm, "end": v(6.59, -13.42) * mm});
            skArc(sketch, "E71.52.startCap", {"start": v(-3.63, -4.67) * mm, "mid": v(-3.13, -5.17) * mm, "end": v(-3.63, -5.67) * mm});
            skArc(sketch, "E71.52.endCap", {"start": v(-14.04, -5.68) * mm, "mid": v(-14.54, -5.18) * mm, "end": v(-14.04, -4.68) * mm});
            skLineSegment(sketch, "E71.52.left", {"start": v(-3.63, -5.67) * mm, "end": v(-14.04, -5.68) * mm});
            skLineSegment(sketch, "E71.52.right", {"start": v(-3.63, -4.67) * mm, "end": v(-14.04, -4.68) * mm});
            skArc(sketch, "E71.53.startCap", {"start": v(-3.63, -17.6) * mm, "mid": v(-3.13, -18.1) * mm, "end": v(-3.63, -18.6) * mm});
            skArc(sketch, "E71.53.endCap", {"start": v(-6.21, -18.6) * mm, "mid": v(-6.71, -18.1) * mm, "end": v(-6.21, -17.6) * mm});
            skLineSegment(sketch, "E71.53.left", {"start": v(-3.63, -18.6) * mm, "end": v(-6.21, -18.6) * mm});
            skLineSegment(sketch, "E71.53.right", {"start": v(-3.63, -17.6) * mm, "end": v(-6.21, -17.6) * mm});
            skArc(sketch, "E71.54.startCap", {"start": v(9.22, -20.23) * mm, "mid": v(9.72, -20.73) * mm, "end": v(9.22, -21.23) * mm});
            skArc(sketch, "E71.54.endCap", {"start": v(6.63, -21.23) * mm, "mid": v(6.13, -20.73) * mm, "end": v(6.63, -20.23) * mm});
            skLineSegment(sketch, "E71.54.left", {"start": v(9.22, -21.23) * mm, "end": v(6.63, -21.23) * mm});
            skLineSegment(sketch, "E71.54.right", {"start": v(9.22, -20.23) * mm, "end": v(6.63, -20.23) * mm});
            skArc(sketch, "E71.55.startCap", {"start": v(13.97, -5.17) * mm, "mid": v(14.47, -4.67) * mm, "end": v(14.97, -5.17) * mm});
            skArc(sketch, "E71.55.endCap", {"start": v(14.97, -25.82) * mm, "mid": v(14.47, -26.32) * mm, "end": v(13.97, -25.82) * mm});
            skLineSegment(sketch, "E71.55.left", {"start": v(14.97, -5.17) * mm, "end": v(14.97, -25.82) * mm});
            skLineSegment(sketch, "E71.55.right", {"start": v(13.97, -5.17) * mm, "end": v(13.97, -25.82) * mm});
            skArc(sketch, "E71.56.startCap", {"start": v(-0.63, -25.82) * mm, "mid": v(-1.13, -26.32) * mm, "end": v(-1.63, -25.82) * mm});
            skArc(sketch, "E71.56.endCap", {"start": v(-1.63, -15.5) * mm, "mid": v(-1.13, -15) * mm, "end": v(-0.63, -15.5) * mm});
            skLineSegment(sketch, "E71.56.left", {"start": v(-1.63, -25.82) * mm, "end": v(-1.63, -15.5) * mm});
            skLineSegment(sketch, "E71.56.right", {"start": v(-0.63, -25.82) * mm, "end": v(-0.63, -15.5) * mm});
            skArc(sketch, "E71.57.startCap", {"start": v(-14.04, 30.58) * mm, "mid": v(-14.54, 31.08) * mm, "end": v(-14.04, 31.58) * mm});
            skArc(sketch, "E71.57.endCap", {"start": v(-8.84, 31.58) * mm, "mid": v(-8.34, 31.08) * mm, "end": v(-8.84, 30.58) * mm});
            skLineSegment(sketch, "E71.57.left", {"start": v(-14.04, 31.58) * mm, "end": v(-8.84, 31.58) * mm});
            skLineSegment(sketch, "E71.57.right", {"start": v(-14.04, 30.58) * mm, "end": v(-8.84, 30.58) * mm});
            skArc(sketch, "E71.58.startCap", {"start": v(6.59, -17.64) * mm, "mid": v(7.09, -18.14) * mm, "end": v(6.59, -18.64) * mm});
            skArc(sketch, "E71.58.endCap", {"start": v(4.07, -18.64) * mm, "mid": v(3.57, -18.14) * mm, "end": v(4.07, -17.64) * mm});
            skLineSegment(sketch, "E71.58.left", {"start": v(6.59, -18.64) * mm, "end": v(4.07, -18.64) * mm});
            skLineSegment(sketch, "E71.58.right", {"start": v(6.59, -17.64) * mm, "end": v(4.07, -17.64) * mm});
            skArc(sketch, "E71.59.startCap", {"start": v(4.07, -5.67) * mm, "mid": v(3.57, -5.17) * mm, "end": v(4.07, -4.67) * mm});
            skArc(sketch, "E71.59.endCap", {"start": v(14.47, -4.67) * mm, "mid": v(14.97, -5.17) * mm, "end": v(14.47, -5.67) * mm});
            skLineSegment(sketch, "E71.59.left", {"start": v(4.07, -4.67) * mm, "end": v(14.47, -4.67) * mm});
            skLineSegment(sketch, "E71.59.right", {"start": v(4.07, -5.67) * mm, "end": v(14.47, -5.67) * mm});
            skArc(sketch, "E71.60.startCap", {"start": v(-3.63, 8.37) * mm, "mid": v(-3.13, 7.87) * mm, "end": v(-3.63, 7.37) * mm});
            skArc(sketch, "E71.60.endCap", {"start": v(-14.04, 7.37) * mm, "mid": v(-14.54, 7.87) * mm, "end": v(-14.04, 8.37) * mm});
            skLineSegment(sketch, "E71.60.left", {"start": v(-3.63, 7.37) * mm, "end": v(-14.04, 7.37) * mm});
            skLineSegment(sketch, "E71.60.right", {"start": v(-3.63, 8.37) * mm, "end": v(-14.04, 8.37) * mm});
            skArc(sketch, "E71.61.startCap", {"start": v(-6.24, 28.94) * mm, "mid": v(-5.74, 28.44) * mm, "end": v(-6.24, 27.94) * mm});
            skArc(sketch, "E71.61.endCap", {"start": v(-16.57, 27.94) * mm, "mid": v(-17.07, 28.44) * mm, "end": v(-16.57, 28.94) * mm});
            skLineSegment(sketch, "E71.61.left", {"start": v(-6.24, 27.94) * mm, "end": v(-16.57, 27.94) * mm});
            skLineSegment(sketch, "E71.61.right", {"start": v(-6.24, 28.94) * mm, "end": v(-16.57, 28.94) * mm});
            skArc(sketch, "E71.62.startCap", {"start": v(3.57, -18.14) * mm, "mid": v(4.07, -17.64) * mm, "end": v(4.57, -18.14) * mm});
            skArc(sketch, "E71.62.endCap", {"start": v(4.57, -25.82) * mm, "mid": v(4.07, -26.32) * mm, "end": v(3.57, -25.82) * mm});
            skLineSegment(sketch, "E71.62.left", {"start": v(4.57, -18.14) * mm, "end": v(4.57, -25.82) * mm});
            skLineSegment(sketch, "E71.62.right", {"start": v(3.57, -18.14) * mm, "end": v(3.57, -25.82) * mm});
            skArc(sketch, "E71.63.startCap", {"start": v(-3.63, -12.42) * mm, "mid": v(-3.13, -12.92) * mm, "end": v(-3.63, -13.42) * mm});
            skArc(sketch, "E71.63.endCap", {"start": v(-6.21, -13.42) * mm, "mid": v(-6.71, -12.92) * mm, "end": v(-6.21, -12.42) * mm});
            skLineSegment(sketch, "E71.63.left", {"start": v(-3.63, -13.42) * mm, "end": v(-6.21, -13.42) * mm});
            skLineSegment(sketch, "E71.63.right", {"start": v(-3.63, -12.42) * mm, "end": v(-6.21, -12.42) * mm});
            skArc(sketch, "E71.64.startCap", {"start": v(4.07, -10.8) * mm, "mid": v(3.57, -10.3) * mm, "end": v(4.07, -9.8) * mm});
            skArc(sketch, "E71.64.endCap", {"start": v(9.22, -9.8) * mm, "mid": v(9.72, -10.3) * mm, "end": v(9.22, -10.8) * mm});
            skLineSegment(sketch, "E71.64.left", {"start": v(4.07, -9.8) * mm, "end": v(9.22, -9.8) * mm});
            skLineSegment(sketch, "E71.64.right", {"start": v(4.07, -10.8) * mm, "end": v(9.22, -10.8) * mm});
            skArc(sketch, "E71.65.startCap", {"start": v(-10.87, -23.45) * mm, "mid": v(-11.37, -23.95) * mm, "end": v(-11.87, -23.45) * mm});
            skArc(sketch, "E71.65.endCap", {"start": v(-11.87, -7.68) * mm, "mid": v(-11.37, -7.18) * mm, "end": v(-10.87, -7.68) * mm});
            skLineSegment(sketch, "E71.65.left", {"start": v(-11.87, -23.45) * mm, "end": v(-11.87, -7.68) * mm});
            skLineSegment(sketch, "E71.65.right", {"start": v(-10.87, -23.45) * mm, "end": v(-10.87, -7.68) * mm});
            skSolve(sketch);
        }
        {
            var Q0;
            Q0=makeQuery(id+"F0.imprint","IMPRINT",FACE,{"disambiguationData":[TD([[makeQuery(id+"F0.imprint","IMPRINT",EDGE,{"derivedFrom":sQuery(id+"F0.wireOp",EDGE,"E0.top")}),1.0]])]});
            var sketch = newSketch(context, id + "F2", { "sketchPlane" : qUnion([Q0])});
            skPoint(sketch, "E72", {"position": v(-19.17, 31.12) * mm});
            skPoint(sketch, "E73", {"position": v(-19.17, 18.12) * mm});
            skPoint(sketch, "E74", {"position": v(-19.17, 15.55) * mm});
            skPoint(sketch, "E75", {"position": v(-19.17, 12.96) * mm});
            skPoint(sketch, "E76", {"position": v(-19.17, 10.38) * mm});
            skPoint(sketch, "E77", {"position": v(-19.17, 7.83) * mm});
            skPoint(sketch, "E78", {"position": v(-19.17, 5.26) * mm});
            skPoint(sketch, "E79", {"position": v(-19.17, 2.67) * mm});
            skPoint(sketch, "E80", {"position": v(-16.64, -30.96) * mm});
            skPoint(sketch, "E81", {"position": v(-16.64, -25.77) * mm});
            skPoint(sketch, "E82", {"position": v(-16.64, -5.14) * mm});
            skPoint(sketch, "E83", {"position": v(-16.64, -2.53) * mm});
            skPoint(sketch, "E84", {"position": v(-16.64, 5.26) * mm});
            skPoint(sketch, "E85", {"position": v(-16.64, 7.83) * mm});
            skPoint(sketch, "E86", {"position": v(-16.64, 10.38) * mm});
            skPoint(sketch, "E87", {"position": v(-16.64, 12.96) * mm});
            skPoint(sketch, "E88", {"position": v(-16.64, 15.55) * mm});
            skPoint(sketch, "E89", {"position": v(-14.04, 31.12) * mm});
            skPoint(sketch, "E90", {"position": v(-14.04, 18.12) * mm});
            skPoint(sketch, "E91", {"position": v(-8.87, 31.12) * mm});
            skPoint(sketch, "E92", {"position": v(-8.87, 33.65) * mm});
            skPoint(sketch, "E93", {"position": v(-14.04, 15.55) * mm});
            skPoint(sketch, "E94", {"position": v(-14.04, 12.96) * mm});
            skPoint(sketch, "E95", {"position": v(-14.04, 10.38) * mm});
            skPoint(sketch, "E96", {"position": v(-3.63, 18.12) * mm});
            skPoint(sketch, "E97", {"position": v(-3.63, 15.55) * mm});
            skPoint(sketch, "E98", {"position": v(-3.63, 12.96) * mm});
            skPoint(sketch, "E99", {"position": v(-3.63, 10.38) * mm});
            skPoint(sketch, "E100", {"position": v(-14.04, 7.83) * mm});
            skPoint(sketch, "E101", {"position": v(-3.63, 7.83) * mm});
            skPoint(sketch, "E102", {"position": v(-14.04, 5.26) * mm});
            skPoint(sketch, "E103", {"position": v(-3.63, 5.26) * mm});
            skPoint(sketch, "E104", {"position": v(-14.04, 2.67) * mm});
            skPoint(sketch, "E105", {"position": v(-3.63, 2.67) * mm});
            skPoint(sketch, "E106", {"position": v(-3.63, 0) * mm});
            skPoint(sketch, "E107", {"position": v(-14.04, -2.53) * mm});
            skPoint(sketch, "E108", {"position": v(-8.87, -2.53) * mm});
            skPoint(sketch, "E109", {"position": v(-3.63, -2.53) * mm});
            skPoint(sketch, "E110", {"position": v(-14.04, -5.14) * mm});
            skPoint(sketch, "E111", {"position": v(-8.87, -5.14) * mm});
            skPoint(sketch, "E112", {"position": v(-3.63, -5.14) * mm});
            skPoint(sketch, "E113", {"position": v(-3.63, -7.65) * mm});
            skPoint(sketch, "E114", {"position": v(-3.63, -10.26) * mm});
            skPoint(sketch, "E115", {"position": v(-3.63, -12.9) * mm});
            skPoint(sketch, "E116", {"position": v(-3.63, -15.47) * mm});
            skPoint(sketch, "E117", {"position": v(-8.87, -25.77) * mm});
            skPoint(sketch, "E118", {"position": v(-8.87, -28.41) * mm});
            skPoint(sketch, "E119", {"position": v(-8.87, -30.95) * mm});
            skPoint(sketch, "E120", {"position": v(-6.26, -25.77) * mm});
            skPoint(sketch, "E121", {"position": v(-3.63, -25.77) * mm});
            skPoint(sketch, "E122", {"position": v(-1.15, -25.77) * mm});
            skPoint(sketch, "E123", {"position": v(1.51, -25.77) * mm});
            skPoint(sketch, "E124", {"position": v(4.11, -25.77) * mm});
            skPoint(sketch, "E125", {"position": v(6.65, -25.77) * mm});
            skPoint(sketch, "E126", {"position": v(9.22, -25.77) * mm});
            skPoint(sketch, "E127", {"position": v(11.85, -25.77) * mm});
            skPoint(sketch, "E128", {"position": v(-6.26, -28.41) * mm});
            skPoint(sketch, "E129", {"position": v(-3.63, -28.41) * mm});
            skPoint(sketch, "E130", {"position": v(-1.15, -28.41) * mm});
            skPoint(sketch, "E131", {"position": v(1.51, -28.41) * mm});
            skPoint(sketch, "E132", {"position": v(4.11, -28.41) * mm});
            skPoint(sketch, "E133", {"position": v(6.65, -28.41) * mm});
            skPoint(sketch, "E134", {"position": v(9.22, -28.41) * mm});
            skPoint(sketch, "E135", {"position": v(11.85, -28.41) * mm});
            skPoint(sketch, "E136", {"position": v(11.85, -30.95) * mm});
            skPoint(sketch, "E137", {"position": v(9.22, -30.95) * mm});
            skPoint(sketch, "E138", {"position": v(6.65, -30.95) * mm});
            skPoint(sketch, "E139", {"position": v(4.11, -30.95) * mm});
            skPoint(sketch, "E140", {"position": v(1.51, -30.95) * mm});
            skPoint(sketch, "E141", {"position": v(-1.15, -30.95) * mm});
            skPoint(sketch, "E142", {"position": v(-3.63, -30.95) * mm});
            skPoint(sketch, "E143", {"position": v(-6.26, -30.95) * mm});
            skPoint(sketch, "E144", {"position": v(4.11, -15.47) * mm});
            skPoint(sketch, "E145", {"position": v(4.11, -12.9) * mm});
            skPoint(sketch, "E146", {"position": v(4.11, -10.26) * mm});
            skPoint(sketch, "E147", {"position": v(4.11, -7.65) * mm});
            skPoint(sketch, "E148", {"position": v(4.11, -5.14) * mm});
            skPoint(sketch, "E149", {"position": v(4.11, -2.53) * mm});
            skPoint(sketch, "E150", {"position": v(4.11, 0) * mm});
            skPoint(sketch, "E151", {"position": v(4.11, 10.38) * mm});
            skPoint(sketch, "E152", {"position": v(4.11, 7.83) * mm});
            skPoint(sketch, "E153", {"position": v(4.11, 5.26) * mm});
            skPoint(sketch, "E154", {"position": v(4.11, 2.67) * mm});
            skPoint(sketch, "E155", {"position": v(4.11, 12.96) * mm});
            skPoint(sketch, "E156", {"position": v(4.11, 15.55) * mm});
            skPoint(sketch, "E157", {"position": v(4.11, 18.12) * mm});
            skPoint(sketch, "E158", {"position": v(14.4, 18.12) * mm});
            skPoint(sketch, "E159", {"position": v(14.4, 15.55) * mm});
            skPoint(sketch, "E160", {"position": v(14.4, 12.96) * mm});
            skPoint(sketch, "E161", {"position": v(14.4, 10.38) * mm});
            skPoint(sketch, "E162", {"position": v(14.4, 7.83) * mm});
            skPoint(sketch, "E163", {"position": v(14.4, 5.26) * mm});
            skPoint(sketch, "E164", {"position": v(11.85, 2.67) * mm});
            skPoint(sketch, "E165", {"position": v(16.97, 5.26) * mm});
            skPoint(sketch, "E166", {"position": v(19.58, 5.26) * mm});
            skPoint(sketch, "E167", {"position": v(19.58, 7.83) * mm});
            skPoint(sketch, "E168", {"position": v(19.58, 10.38) * mm});
            skPoint(sketch, "E169", {"position": v(19.58, 12.96) * mm});
            skPoint(sketch, "E170", {"position": v(19.58, 15.55) * mm});
            skPoint(sketch, "E171", {"position": v(19.58, 18.12) * mm});
            skPoint(sketch, "E172", {"position": v(16.97, 18.12) * mm});
            skPoint(sketch, "E173", {"position": v(16.97, 15.55) * mm});
            skPoint(sketch, "E174", {"position": v(16.97, 12.96) * mm});
            skPoint(sketch, "E175", {"position": v(16.97, 10.38) * mm});
            skPoint(sketch, "E176", {"position": v(16.97, 7.83) * mm});
            skPoint(sketch, "E177", {"position": v(16.97, 23.33) * mm});
            skPoint(sketch, "E178", {"position": v(19.58, 23.38) * mm});
            skPoint(sketch, "E179", {"position": v(11.84, 28.46) * mm});
            skPoint(sketch, "E180", {"position": v(11.81, 31.12) * mm});
            skPoint(sketch, "E181", {"position": v(11.87, 33.62) * mm});
            skPoint(sketch, "E182", {"position": v(6.6, 33.62) * mm});
            skPoint(sketch, "E183", {"position": v(6.6, 31.12) * mm});
            skPoint(sketch, "E184", {"position": v(1.44, 31.12) * mm});
            skPoint(sketch, "E185", {"position": v(1.44, 33.62) * mm});
            skPoint(sketch, "E186", {"position": v(-6.27, 28.46) * mm});
            skPoint(sketch, "E187", {"position": v(-6.27, 23.33) * mm});
            skPoint(sketch, "E188", {"position": v(19.58, 2.67) * mm});
            skSolve(sketch);
        }
        {
            var Q0;
            Q0=makeQuery(id+"F0.imprint","IMPRINT",FACE,{"disambiguationData":[TD([[makeQuery(id+"F0.imprint","IMPRINT",EDGE,{"derivedFrom":sQuery(id+"F0.wireOp",EDGE,"E0.top")}),1.0]])]});
            extrude(context, id + "F3", {"entities" : qUnion([Q0]), "oppositeDirection" : true, "depth" : 2 * mm, "offsetDistance" : 25 * mm});
        }
        {
            var Q0;
            Q0 = qSketchRegion(id + "F1", true);
            extrude(context, id + "F4", {"entities" : qUnion([Q0]), "operationType" : NewBodyOperationType.REMOVE, "oppositeDirection" : true, "depth" : 1 * mm, "offsetDistance" : 25 * mm});
        }
        {
            var Q0;
            Q0 = qSketchRegion(id + "F1", true);
            extrude(context, id + "F5", {"entities" : qUnion([Q0]), "oppositeDirection" : true, "depth" : 1 * mm, "offsetDistance" : 25 * mm});
        }
        {
            var Q0;
            Q0=sQuery(id+"F2.wireOp",VERTEX,"E118");
            var Q1;
            Q1=sQuery(id+"F2.wireOp",VERTEX,"E72");
            var Q2;
            Q2=sQuery(id+"F2.wireOp",VERTEX,"E85");
            var Q3;
            Q3=sQuery(id+"F2.wireOp",VERTEX,"E83");
            var Q4;
            Q4=sQuery(id+"F2.wireOp",VERTEX,"E84");
            var Q5;
            Q5=sQuery(id+"F2.wireOp",VERTEX,"E82");
            var Q6;
            Q6=sQuery(id+"F2.wireOp",VERTEX,"E81");
            var Q7;
            Q7=sQuery(id+"F2.wireOp",VERTEX,"E77");
            var Q8;
            Q8=sQuery(id+"F2.wireOp",VERTEX,"E73");
            var Q9;
            Q9=sQuery(id+"F2.wireOp",VERTEX,"E86");
            var Q10;
            Q10=sQuery(id+"F2.wireOp",VERTEX,"E87");
            var Q11;
            Q11=sQuery(id+"F2.wireOp",VERTEX,"E80");
            var Q12;
            Q12=sQuery(id+"F2.wireOp",VERTEX,"E76");
            var Q13;
            Q13=sQuery(id+"F2.wireOp",VERTEX,"E78");
            var Q14;
            Q14=sQuery(id+"F2.wireOp",VERTEX,"E79");
            var Q15;
            Q15=sQuery(id+"F2.wireOp",VERTEX,"E74");
            var Q16;
            Q16=sQuery(id+"F2.wireOp",VERTEX,"E75");
            var Q17;
            Q17=sQuery(id+"F2.wireOp",VERTEX,"E111");
            var Q18;
            Q18=sQuery(id+"F2.wireOp",VERTEX,"E95");
            var Q19;
            Q19=sQuery(id+"F2.wireOp",VERTEX,"E112");
            var Q20;
            Q20=sQuery(id+"F2.wireOp",VERTEX,"E143");
            var Q21;
            Q21=sQuery(id+"F2.wireOp",VERTEX,"E142");
            var Q22;
            Q22=sQuery(id+"F2.wireOp",VERTEX,"E110");
            var Q23;
            Q23=sQuery(id+"F2.wireOp",VERTEX,"E94");
            var Q24;
            Q24=sQuery(id+"F2.wireOp",VERTEX,"E100");
            var Q25;
            Q25=sQuery(id+"F2.wireOp",VERTEX,"E99");
            var Q26;
            Q26=sQuery(id+"F2.wireOp",VERTEX,"E113");
            var Q27;
            Q27=sQuery(id+"F2.wireOp",VERTEX,"E98");
            var Q28;
            Q28=sQuery(id+"F2.wireOp",VERTEX,"E128");
            var Q29;
            Q29=sQuery(id+"F2.wireOp",VERTEX,"E116");
            var Q30;
            Q30=sQuery(id+"F2.wireOp",VERTEX,"E130");
            var Q31;
            Q31=sQuery(id+"F2.wireOp",VERTEX,"E115");
            var Q32;
            Q32=sQuery(id+"F2.wireOp",VERTEX,"E97");
            var Q33;
            Q33=sQuery(id+"F2.wireOp",VERTEX,"E129");
            var Q34;
            Q34=sQuery(id+"F2.wireOp",VERTEX,"E114");
            var Q35;
            Q35=sQuery(id+"F2.wireOp",VERTEX,"E96");
            var Q36;
            Q36=sQuery(id+"F2.wireOp",VERTEX,"E109");
            var Q37;
            Q37=sQuery(id+"F2.wireOp",VERTEX,"E93");
            var Q38;
            Q38=sQuery(id+"F2.wireOp",VERTEX,"E187");
            var Q39;
            Q39=sQuery(id+"F2.wireOp",VERTEX,"E107");
            var Q40;
            Q40=sQuery(id+"F2.wireOp",VERTEX,"E91");
            var Q41;
            Q41=sQuery(id+"F2.wireOp",VERTEX,"E141");
            var Q42;
            Q42=sQuery(id+"F2.wireOp",VERTEX,"E108");
            var Q43;
            Q43=sQuery(id+"F2.wireOp",VERTEX,"E92");
            var Q44;
            Q44=sQuery(id+"F2.wireOp",VERTEX,"E121");
            var Q45;
            Q45=sQuery(id+"F2.wireOp",VERTEX,"E105");
            var Q46;
            Q46=sQuery(id+"F2.wireOp",VERTEX,"E89");
            var Q47;
            Q47=sQuery(id+"F2.wireOp",VERTEX,"E120");
            var Q48;
            Q48=sQuery(id+"F2.wireOp",VERTEX,"E104");
            var Q49;
            Q49=sQuery(id+"F2.wireOp",VERTEX,"E88");
            var Q50;
            Q50=sQuery(id+"F2.wireOp",VERTEX,"E106");
            var Q51;
            Q51=sQuery(id+"F2.wireOp",VERTEX,"E90");
            var Q52;
            Q52=sQuery(id+"F2.wireOp",VERTEX,"E186");
            var Q53;
            Q53=sQuery(id+"F2.wireOp",VERTEX,"E122");
            var Q54;
            Q54=sQuery(id+"F2.wireOp",VERTEX,"E119");
            var Q55;
            Q55=sQuery(id+"F2.wireOp",VERTEX,"E103");
            var Q56;
            Q56=sQuery(id+"F2.wireOp",VERTEX,"E102");
            var Q57;
            Q57=sQuery(id+"F2.wireOp",VERTEX,"E101");
            var Q58;
            Q58=sQuery(id+"F2.wireOp",VERTEX,"E117");
            var Q59;
            Q59=makeQuery(id+"F3.opExtrude","SWEPT_BODY",BODY,{"disambiguationData":[OSD([sQuery(id+"F0.wireOp",EDGE,"E0.bottom"),sQuery(id+"F0.wireOp",EDGE,"E0.top"),sQuery(id+"F0.wireOp",EDGE,"E0.left"),sQuery(id+"F0.wireOp",EDGE,"E0.right")])]});
            var Q60;
            Q60=makeQuery(id+"F5.opExtrude","SWEPT_BODY",BODY,{"disambiguationData":[OSD([sQuery(id+"F1.wireOp",EDGE,"E71.17.startCap"),sQuery(id+"F1.wireOp",EDGE,"E71.17.left"),sQuery(id+"F1.wireOp",EDGE,"E71.17.right"),sQuery(id+"F1.wireOp",EDGE,"E71.18.startCap"),sQuery(id+"F1.wireOp",EDGE,"E71.18.left"),sQuery(id+"F1.wireOp",EDGE,"E71.18.right"),sQuery(id+"F1.wireOp",EDGE,"E71.25.startCap"),sQuery(id+"F1.wireOp",EDGE,"E71.25.left"),sQuery(id+"F1.wireOp",EDGE,"E71.25.right"),sQuery(id+"F1.wireOp",EDGE,"E71.34.left"),sQuery(id+"F1.wireOp",EDGE,"E71.34.right"),sQuery(id+"F1.wireOp",EDGE,"E71.41.startCap"),sQuery(id+"F1.wireOp",EDGE,"E71.41.endCap"),sQuery(id+"F1.wireOp",EDGE,"E71.41.left"),sQuery(id+"F1.wireOp",EDGE,"E71.41.right"),sQuery(id+"F1.wireOp",EDGE,"E71.45.startCap"),sQuery(id+"F1.wireOp",EDGE,"E71.45.endCap"),sQuery(id+"F1.wireOp",EDGE,"E71.45.left"),sQuery(id+"F1.wireOp",EDGE,"E71.45.right")])]});
            var Q61;
            Q61=makeQuery(id+"F5.opExtrude","SWEPT_BODY",BODY,{"disambiguationData":[OSD([sQuery(id+"F1.wireOp",EDGE,"E71.0.startCap"),sQuery(id+"F1.wireOp",EDGE,"E71.0.left"),sQuery(id+"F1.wireOp",EDGE,"E71.0.right"),sQuery(id+"F1.wireOp",EDGE,"E71.2.endCap"),sQuery(id+"F1.wireOp",EDGE,"E71.2.left"),sQuery(id+"F1.wireOp",EDGE,"E71.2.right"),sQuery(id+"F1.wireOp",EDGE,"E71.14.left"),sQuery(id+"F1.wireOp",EDGE,"E71.14.right"),sQuery(id+"F1.wireOp",EDGE,"E71.15.startCap"),sQuery(id+"F1.wireOp",EDGE,"E71.15.left"),sQuery(id+"F1.wireOp",EDGE,"E71.15.right"),sQuery(id+"F1.wireOp",EDGE,"E71.23.startCap"),sQuery(id+"F1.wireOp",EDGE,"E71.23.left"),sQuery(id+"F1.wireOp",EDGE,"E71.23.right"),sQuery(id+"F1.wireOp",EDGE,"E71.24.startCap"),sQuery(id+"F1.wireOp",EDGE,"E71.24.endCap"),sQuery(id+"F1.wireOp",EDGE,"E71.24.left"),sQuery(id+"F1.wireOp",EDGE,"E71.24.right"),sQuery(id+"F1.wireOp",EDGE,"E71.27.startCap"),sQuery(id+"F1.wireOp",EDGE,"E71.27.left"),sQuery(id+"F1.wireOp",EDGE,"E71.27.right"),sQuery(id+"F1.wireOp",EDGE,"E71.35.startCap"),sQuery(id+"F1.wireOp",EDGE,"E71.35.left"),sQuery(id+"F1.wireOp",EDGE,"E71.35.right"),sQuery(id+"F1.wireOp",EDGE,"E71.36.endCap"),sQuery(id+"F1.wireOp",EDGE,"E71.36.left"),sQuery(id+"F1.wireOp",EDGE,"E71.36.right"),sQuery(id+"F1.wireOp",EDGE,"E71.39.startCap"),sQuery(id+"F1.wireOp",EDGE,"E71.39.left"),sQuery(id+"F1.wireOp",EDGE,"E71.39.right"),sQuery(id+"F1.wireOp",EDGE,"E71.42.startCap"),sQuery(id+"F1.wireOp",EDGE,"E71.42.left"),sQuery(id+"F1.wireOp",EDGE,"E71.42.right"),sQuery(id+"F1.wireOp",EDGE,"E71.48.startCap"),sQuery(id+"F1.wireOp",EDGE,"E71.48.left"),sQuery(id+"F1.wireOp",EDGE,"E71.48.right"),sQuery(id+"F1.wireOp",EDGE,"E71.50.endCap"),sQuery(id+"F1.wireOp",EDGE,"E71.50.left"),sQuery(id+"F1.wireOp",EDGE,"E71.50.right"),sQuery(id+"F1.wireOp",EDGE,"E71.52.startCap"),sQuery(id+"F1.wireOp",EDGE,"E71.52.endCap"),sQuery(id+"F1.wireOp",EDGE,"E71.52.left"),sQuery(id+"F1.wireOp",EDGE,"E71.52.right"),sQuery(id+"F1.wireOp",EDGE,"E71.60.startCap"),sQuery(id+"F1.wireOp",EDGE,"E71.60.left"),sQuery(id+"F1.wireOp",EDGE,"E71.60.right"),sQuery(id+"F1.wireOp",EDGE,"E71.61.startCap"),sQuery(id+"F1.wireOp",EDGE,"E71.61.left"),sQuery(id+"F1.wireOp",EDGE,"E71.61.right")])]});
            var Q62;
            Q62=makeQuery(id+"F5.opExtrude","SWEPT_BODY",BODY,{"disambiguationData":[OSD([sQuery(id+"F1.wireOp",EDGE,"E71.8.endCap"),sQuery(id+"F1.wireOp",EDGE,"E71.8.left"),sQuery(id+"F1.wireOp",EDGE,"E71.8.right"),sQuery(id+"F1.wireOp",EDGE,"E71.31.startCap"),sQuery(id+"F1.wireOp",EDGE,"E71.31.left"),sQuery(id+"F1.wireOp",EDGE,"E71.31.right"),sQuery(id+"F1.wireOp",EDGE,"E71.43.startCap"),sQuery(id+"F1.wireOp",EDGE,"E71.43.endCap"),sQuery(id+"F1.wireOp",EDGE,"E71.43.left"),sQuery(id+"F1.wireOp",EDGE,"E71.43.right")])]});
            var Q63;
            Q63=makeQuery(id+"F5.opExtrude","SWEPT_BODY",BODY,{"disambiguationData":[OSD([sQuery(id+"F1.wireOp",EDGE,"E71.1.left"),sQuery(id+"F1.wireOp",EDGE,"E71.1.right"),sQuery(id+"F1.wireOp",EDGE,"E71.4.left"),sQuery(id+"F1.wireOp",EDGE,"E71.4.right"),sQuery(id+"F1.wireOp",EDGE,"E71.5.left"),sQuery(id+"F1.wireOp",EDGE,"E71.5.right"),sQuery(id+"F1.wireOp",EDGE,"E71.6.startCap"),sQuery(id+"F1.wireOp",EDGE,"E71.6.left"),sQuery(id+"F1.wireOp",EDGE,"E71.6.right"),sQuery(id+"F1.wireOp",EDGE,"E71.7.left"),sQuery(id+"F1.wireOp",EDGE,"E71.7.right"),sQuery(id+"F1.wireOp",EDGE,"E71.9.startCap"),sQuery(id+"F1.wireOp",EDGE,"E71.9.left"),sQuery(id+"F1.wireOp",EDGE,"E71.9.right"),sQuery(id+"F1.wireOp",EDGE,"E71.10.left"),sQuery(id+"F1.wireOp",EDGE,"E71.10.right"),sQuery(id+"F1.wireOp",EDGE,"E71.11.left"),sQuery(id+"F1.wireOp",EDGE,"E71.11.right"),sQuery(id+"F1.wireOp",EDGE,"E71.12.startCap"),sQuery(id+"F1.wireOp",EDGE,"E71.12.endCap"),sQuery(id+"F1.wireOp",EDGE,"E71.12.left"),sQuery(id+"F1.wireOp",EDGE,"E71.12.right"),sQuery(id+"F1.wireOp",EDGE,"E71.16.startCap"),sQuery(id+"F1.wireOp",EDGE,"E71.16.left"),sQuery(id+"F1.wireOp",EDGE,"E71.16.right"),sQuery(id+"F1.wireOp",EDGE,"E71.19.startCap"),sQuery(id+"F1.wireOp",EDGE,"E71.19.endCap"),sQuery(id+"F1.wireOp",EDGE,"E71.19.left"),sQuery(id+"F1.wireOp",EDGE,"E71.19.right"),sQuery(id+"F1.wireOp",EDGE,"E71.21.endCap"),sQuery(id+"F1.wireOp",EDGE,"E71.21.left"),sQuery(id+"F1.wireOp",EDGE,"E71.21.right"),sQuery(id+"F1.wireOp",EDGE,"E71.26.startCap"),sQuery(id+"F1.wireOp",EDGE,"E71.26.left"),sQuery(id+"F1.wireOp",EDGE,"E71.26.right"),sQuery(id+"F1.wireOp",EDGE,"E71.30.startCap"),sQuery(id+"F1.wireOp",EDGE,"E71.30.left"),sQuery(id+"F1.wireOp",EDGE,"E71.30.right"),sQuery(id+"F1.wireOp",EDGE,"E71.32.left"),sQuery(id+"F1.wireOp",EDGE,"E71.32.right"),sQuery(id+"F1.wireOp",EDGE,"E71.33.endCap"),sQuery(id+"F1.wireOp",EDGE,"E71.33.left"),sQuery(id+"F1.wireOp",EDGE,"E71.33.right"),sQuery(id+"F1.wireOp",EDGE,"E71.37.left"),sQuery(id+"F1.wireOp",EDGE,"E71.37.right"),sQuery(id+"F1.wireOp",EDGE,"E71.38.startCap"),sQuery(id+"F1.wireOp",EDGE,"E71.38.endCap"),sQuery(id+"F1.wireOp",EDGE,"E71.38.left"),sQuery(id+"F1.wireOp",EDGE,"E71.38.right"),sQuery(id+"F1.wireOp",EDGE,"E71.46.startCap"),sQuery(id+"F1.wireOp",EDGE,"E71.46.left"),sQuery(id+"F1.wireOp",EDGE,"E71.46.right"),sQuery(id+"F1.wireOp",EDGE,"E71.47.left"),sQuery(id+"F1.wireOp",EDGE,"E71.47.right"),sQuery(id+"F1.wireOp",EDGE,"E71.49.left"),sQuery(id+"F1.wireOp",EDGE,"E71.49.right"),sQuery(id+"F1.wireOp",EDGE,"E71.51.startCap"),sQuery(id+"F1.wireOp",EDGE,"E71.51.endCap"),sQuery(id+"F1.wireOp",EDGE,"E71.51.left"),sQuery(id+"F1.wireOp",EDGE,"E71.51.right"),sQuery(id+"F1.wireOp",EDGE,"E71.53.startCap"),sQuery(id+"F1.wireOp",EDGE,"E71.53.endCap"),sQuery(id+"F1.wireOp",EDGE,"E71.53.left"),sQuery(id+"F1.wireOp",EDGE,"E71.53.right"),sQuery(id+"F1.wireOp",EDGE,"E71.54.startCap"),sQuery(id+"F1.wireOp",EDGE,"E71.54.endCap"),sQuery(id+"F1.wireOp",EDGE,"E71.54.left"),sQuery(id+"F1.wireOp",EDGE,"E71.54.right"),sQuery(id+"F1.wireOp",EDGE,"E71.55.endCap"),sQuery(id+"F1.wireOp",EDGE,"E71.55.left"),sQuery(id+"F1.wireOp",EDGE,"E71.55.right"),sQuery(id+"F1.wireOp",EDGE,"E71.56.endCap"),sQuery(id+"F1.wireOp",EDGE,"E71.56.left"),sQuery(id+"F1.wireOp",EDGE,"E71.56.right"),sQuery(id+"F1.wireOp",EDGE,"E71.58.startCap"),sQuery(id+"F1.wireOp",EDGE,"E71.58.left"),sQuery(id+"F1.wireOp",EDGE,"E71.58.right"),sQuery(id+"F1.wireOp",EDGE,"E71.59.startCap"),sQuery(id+"F1.wireOp",EDGE,"E71.59.endCap"),sQuery(id+"F1.wireOp",EDGE,"E71.59.left"),sQuery(id+"F1.wireOp",EDGE,"E71.59.right"),sQuery(id+"F1.wireOp",EDGE,"E71.62.startCap"),sQuery(id+"F1.wireOp",EDGE,"E71.62.left"),sQuery(id+"F1.wireOp",EDGE,"E71.62.right"),sQuery(id+"F1.wireOp",EDGE,"E71.63.startCap"),sQuery(id+"F1.wireOp",EDGE,"E71.63.endCap"),sQuery(id+"F1.wireOp",EDGE,"E71.63.left"),sQuery(id+"F1.wireOp",EDGE,"E71.63.right"),sQuery(id+"F1.wireOp",EDGE,"E71.64.startCap"),sQuery(id+"F1.wireOp",EDGE,"E71.64.endCap"),sQuery(id+"F1.wireOp",EDGE,"E71.64.left"),sQuery(id+"F1.wireOp",EDGE,"E71.64.right"),sQuery(id+"F1.wireOp",EDGE,"E71.65.startCap"),sQuery(id+"F1.wireOp",EDGE,"E71.65.endCap"),sQuery(id+"F1.wireOp",EDGE,"E71.65.left"),sQuery(id+"F1.wireOp",EDGE,"E71.65.right")])]});
            var Q64;
            Q64=makeQuery(id+"F5.opExtrude","SWEPT_BODY",BODY,{"disambiguationData":[OSD([sQuery(id+"F1.wireOp",EDGE,"E71.29.startCap"),sQuery(id+"F1.wireOp",EDGE,"E71.29.endCap"),sQuery(id+"F1.wireOp",EDGE,"E71.29.left"),sQuery(id+"F1.wireOp",EDGE,"E71.29.right")])]});
            var Q65;
            Q65=makeQuery(id+"F5.opExtrude","SWEPT_BODY",BODY,{"disambiguationData":[OSD([sQuery(id+"F1.wireOp",EDGE,"E71.28.startCap"),sQuery(id+"F1.wireOp",EDGE,"E71.28.endCap"),sQuery(id+"F1.wireOp",EDGE,"E71.28.left"),sQuery(id+"F1.wireOp",EDGE,"E71.28.right")])]});
            var Q66;
            Q66=makeQuery(id+"F5.opExtrude","SWEPT_BODY",BODY,{"disambiguationData":[OSD([sQuery(id+"F1.wireOp",EDGE,"E71.40.startCap"),sQuery(id+"F1.wireOp",EDGE,"E71.40.endCap"),sQuery(id+"F1.wireOp",EDGE,"E71.40.left"),sQuery(id+"F1.wireOp",EDGE,"E71.40.right")])]});
            var Q67;
            Q67=makeQuery(id+"F5.opExtrude","SWEPT_BODY",BODY,{"disambiguationData":[OSD([sQuery(id+"F1.wireOp",EDGE,"E71.20.startCap"),sQuery(id+"F1.wireOp",EDGE,"E71.20.endCap"),sQuery(id+"F1.wireOp",EDGE,"E71.20.left"),sQuery(id+"F1.wireOp",EDGE,"E71.20.right")])]});
            var Q68;
            Q68=makeQuery(id+"F5.opExtrude","SWEPT_BODY",BODY,{"disambiguationData":[OSD([sQuery(id+"F1.wireOp",EDGE,"E71.22.startCap"),sQuery(id+"F1.wireOp",EDGE,"E71.22.endCap"),sQuery(id+"F1.wireOp",EDGE,"E71.22.left"),sQuery(id+"F1.wireOp",EDGE,"E71.22.right")])]});
            var Q69;
            Q69=makeQuery(id+"F5.opExtrude","SWEPT_BODY",BODY,{"disambiguationData":[OSD([sQuery(id+"F1.wireOp",EDGE,"E71.13.startCap"),sQuery(id+"F1.wireOp",EDGE,"E71.13.endCap"),sQuery(id+"F1.wireOp",EDGE,"E71.13.left"),sQuery(id+"F1.wireOp",EDGE,"E71.13.right")])]});
            var Q70;
            Q70=makeQuery(id+"F5.opExtrude","SWEPT_BODY",BODY,{"disambiguationData":[OSD([sQuery(id+"F1.wireOp",EDGE,"E71.3.startCap"),sQuery(id+"F1.wireOp",EDGE,"E71.3.endCap"),sQuery(id+"F1.wireOp",EDGE,"E71.3.left"),sQuery(id+"F1.wireOp",EDGE,"E71.3.right")])]});
            var Q71;
            Q71=makeQuery(id+"F5.opExtrude","SWEPT_BODY",BODY,{"disambiguationData":[OSD([sQuery(id+"F1.wireOp",EDGE,"E71.57.startCap"),sQuery(id+"F1.wireOp",EDGE,"E71.57.endCap"),sQuery(id+"F1.wireOp",EDGE,"E71.57.left"),sQuery(id+"F1.wireOp",EDGE,"E71.57.right")])]});
            var Q72;
            Q72=makeQuery(id+"F5.opExtrude","SWEPT_BODY",BODY,{"disambiguationData":[OSD([sQuery(id+"F1.wireOp",EDGE,"E71.44.startCap"),sQuery(id+"F1.wireOp",EDGE,"E71.44.endCap"),sQuery(id+"F1.wireOp",EDGE,"E71.44.left"),sQuery(id+"F1.wireOp",EDGE,"E71.44.right")])]});
            hole(context, id + "F6", {"style" : HoleStyle.SIMPLE, "endStyle" : HoleEndStyle.THROUGH, "holeDiameter" : 1 * mm, "majorDiameter" : 5 * mm, "isTappedThrough" : true, "tappedDepth" : 12 * mm, "tapClearance" : 3, "locations" : qUnion([Q0, Q1, Q2, Q3, Q4, Q5, Q6, Q7, Q8, Q9, Q10, Q11, Q12, Q13, Q14, Q15, Q16, Q17, Q18, Q19, Q20, Q21, Q22, Q23, Q24, Q25, Q26, Q27, Q28, Q29, Q30, Q31, Q32, Q33, Q34, Q35, Q36, Q37, Q38, Q39, Q40, Q41, Q42, Q43, Q44, Q45, Q46, Q47, Q48, Q49, Q50, Q51, Q52, Q53, Q54, Q55, Q56, Q57, Q58]), "scope" : qUnion([Q59, Q60, Q61, Q62, Q63, Q64, Q65, Q66, Q67, Q68, Q69, Q70, Q71, Q72])});
        }
        {
            var Q0;
            Q0=sQuery(id+"F2.wireOp",VERTEX,"E185");
            var Q1;
            Q1=sQuery(id+"F2.wireOp",VERTEX,"E182");
            var Q2;
            Q2=sQuery(id+"F2.wireOp",VERTEX,"E181");
            var Q3;
            Q3=sQuery(id+"F2.wireOp",VERTEX,"E184");
            var Q4;
            Q4=sQuery(id+"F2.wireOp",VERTEX,"E183");
            var Q5;
            Q5=sQuery(id+"F2.wireOp",VERTEX,"E180");
            var Q6;
            Q6=sQuery(id+"F2.wireOp",VERTEX,"E178");
            var Q7;
            Q7=sQuery(id+"F2.wireOp",VERTEX,"E179");
            var Q8;
            Q8=sQuery(id+"F2.wireOp",VERTEX,"E177");
            var Q9;
            Q9=sQuery(id+"F2.wireOp",VERTEX,"E172");
            var Q10;
            Q10=sQuery(id+"F2.wireOp",VERTEX,"E171");
            var Q11;
            Q11=sQuery(id+"F2.wireOp",VERTEX,"E170");
            var Q12;
            Q12=sQuery(id+"F2.wireOp",VERTEX,"E173");
            var Q13;
            Q13=sQuery(id+"F2.wireOp",VERTEX,"E174");
            var Q14;
            Q14=sQuery(id+"F2.wireOp",VERTEX,"E169");
            var Q15;
            Q15=sQuery(id+"F2.wireOp",VERTEX,"E168");
            var Q16;
            Q16=sQuery(id+"F2.wireOp",VERTEX,"E175");
            var Q17;
            Q17=sQuery(id+"F2.wireOp",VERTEX,"E176");
            var Q18;
            Q18=sQuery(id+"F2.wireOp",VERTEX,"E167");
            var Q19;
            Q19=sQuery(id+"F2.wireOp",VERTEX,"E166");
            var Q20;
            Q20=sQuery(id+"F2.wireOp",VERTEX,"E165");
            var Q21;
            Q21=sQuery(id+"F2.wireOp",VERTEX,"E188");
            var Q22;
            Q22=sQuery(id+"F2.wireOp",VERTEX,"E158");
            var Q23;
            Q23=sQuery(id+"F2.wireOp",VERTEX,"E157");
            var Q24;
            Q24=sQuery(id+"F2.wireOp",VERTEX,"E156");
            var Q25;
            Q25=sQuery(id+"F2.wireOp",VERTEX,"E159");
            var Q26;
            Q26=sQuery(id+"F2.wireOp",VERTEX,"E160");
            var Q27;
            Q27=sQuery(id+"F2.wireOp",VERTEX,"E155");
            var Q28;
            Q28=sQuery(id+"F2.wireOp",VERTEX,"E161");
            var Q29;
            Q29=sQuery(id+"F2.wireOp",VERTEX,"E151");
            var Q30;
            Q30=sQuery(id+"F2.wireOp",VERTEX,"E152");
            var Q31;
            Q31=sQuery(id+"F2.wireOp",VERTEX,"E162");
            var Q32;
            Q32=sQuery(id+"F2.wireOp",VERTEX,"E163");
            var Q33;
            Q33=sQuery(id+"F2.wireOp",VERTEX,"E153");
            var Q34;
            Q34=sQuery(id+"F2.wireOp",VERTEX,"E154");
            var Q35;
            Q35=sQuery(id+"F2.wireOp",VERTEX,"E164");
            var Q36;
            Q36=makeQuery(id+"F3.opExtrude","SWEPT_BODY",BODY,{"disambiguationData":[OSD([sQuery(id+"F0.wireOp",EDGE,"E0.bottom"),sQuery(id+"F0.wireOp",EDGE,"E0.top"),sQuery(id+"F0.wireOp",EDGE,"E0.left"),sQuery(id+"F0.wireOp",EDGE,"E0.right")])]});
            var Q37;
            Q37=makeQuery(id+"F5.opExtrude","SWEPT_BODY",BODY,{"disambiguationData":[OSD([sQuery(id+"F1.wireOp",EDGE,"E71.1.left"),sQuery(id+"F1.wireOp",EDGE,"E71.1.right"),sQuery(id+"F1.wireOp",EDGE,"E71.4.left"),sQuery(id+"F1.wireOp",EDGE,"E71.4.right"),sQuery(id+"F1.wireOp",EDGE,"E71.5.left"),sQuery(id+"F1.wireOp",EDGE,"E71.5.right"),sQuery(id+"F1.wireOp",EDGE,"E71.6.startCap"),sQuery(id+"F1.wireOp",EDGE,"E71.6.left"),sQuery(id+"F1.wireOp",EDGE,"E71.6.right"),sQuery(id+"F1.wireOp",EDGE,"E71.7.left"),sQuery(id+"F1.wireOp",EDGE,"E71.7.right"),sQuery(id+"F1.wireOp",EDGE,"E71.9.startCap"),sQuery(id+"F1.wireOp",EDGE,"E71.9.left"),sQuery(id+"F1.wireOp",EDGE,"E71.9.right"),sQuery(id+"F1.wireOp",EDGE,"E71.10.left"),sQuery(id+"F1.wireOp",EDGE,"E71.10.right"),sQuery(id+"F1.wireOp",EDGE,"E71.11.left"),sQuery(id+"F1.wireOp",EDGE,"E71.11.right"),sQuery(id+"F1.wireOp",EDGE,"E71.12.startCap"),sQuery(id+"F1.wireOp",EDGE,"E71.12.endCap"),sQuery(id+"F1.wireOp",EDGE,"E71.12.left"),sQuery(id+"F1.wireOp",EDGE,"E71.12.right"),sQuery(id+"F1.wireOp",EDGE,"E71.16.startCap"),sQuery(id+"F1.wireOp",EDGE,"E71.16.left"),sQuery(id+"F1.wireOp",EDGE,"E71.16.right"),sQuery(id+"F1.wireOp",EDGE,"E71.19.startCap"),sQuery(id+"F1.wireOp",EDGE,"E71.19.endCap"),sQuery(id+"F1.wireOp",EDGE,"E71.19.left"),sQuery(id+"F1.wireOp",EDGE,"E71.19.right"),sQuery(id+"F1.wireOp",EDGE,"E71.21.endCap"),sQuery(id+"F1.wireOp",EDGE,"E71.21.left"),sQuery(id+"F1.wireOp",EDGE,"E71.21.right"),sQuery(id+"F1.wireOp",EDGE,"E71.26.startCap"),sQuery(id+"F1.wireOp",EDGE,"E71.26.left"),sQuery(id+"F1.wireOp",EDGE,"E71.26.right"),sQuery(id+"F1.wireOp",EDGE,"E71.30.startCap"),sQuery(id+"F1.wireOp",EDGE,"E71.30.left"),sQuery(id+"F1.wireOp",EDGE,"E71.30.right"),sQuery(id+"F1.wireOp",EDGE,"E71.32.left"),sQuery(id+"F1.wireOp",EDGE,"E71.32.right"),sQuery(id+"F1.wireOp",EDGE,"E71.33.endCap"),sQuery(id+"F1.wireOp",EDGE,"E71.33.left"),sQuery(id+"F1.wireOp",EDGE,"E71.33.right"),sQuery(id+"F1.wireOp",EDGE,"E71.37.left"),sQuery(id+"F1.wireOp",EDGE,"E71.37.right"),sQuery(id+"F1.wireOp",EDGE,"E71.38.startCap"),sQuery(id+"F1.wireOp",EDGE,"E71.38.endCap"),sQuery(id+"F1.wireOp",EDGE,"E71.38.left"),sQuery(id+"F1.wireOp",EDGE,"E71.38.right"),sQuery(id+"F1.wireOp",EDGE,"E71.46.startCap"),sQuery(id+"F1.wireOp",EDGE,"E71.46.left"),sQuery(id+"F1.wireOp",EDGE,"E71.46.right"),sQuery(id+"F1.wireOp",EDGE,"E71.47.left"),sQuery(id+"F1.wireOp",EDGE,"E71.47.right"),sQuery(id+"F1.wireOp",EDGE,"E71.49.left"),sQuery(id+"F1.wireOp",EDGE,"E71.49.right"),sQuery(id+"F1.wireOp",EDGE,"E71.51.startCap"),sQuery(id+"F1.wireOp",EDGE,"E71.51.endCap"),sQuery(id+"F1.wireOp",EDGE,"E71.51.left"),sQuery(id+"F1.wireOp",EDGE,"E71.51.right"),sQuery(id+"F1.wireOp",EDGE,"E71.53.startCap"),sQuery(id+"F1.wireOp",EDGE,"E71.53.endCap"),sQuery(id+"F1.wireOp",EDGE,"E71.53.left"),sQuery(id+"F1.wireOp",EDGE,"E71.53.right"),sQuery(id+"F1.wireOp",EDGE,"E71.54.startCap"),sQuery(id+"F1.wireOp",EDGE,"E71.54.endCap"),sQuery(id+"F1.wireOp",EDGE,"E71.54.left"),sQuery(id+"F1.wireOp",EDGE,"E71.54.right"),sQuery(id+"F1.wireOp",EDGE,"E71.55.endCap"),sQuery(id+"F1.wireOp",EDGE,"E71.55.left"),sQuery(id+"F1.wireOp",EDGE,"E71.55.right"),sQuery(id+"F1.wireOp",EDGE,"E71.56.endCap"),sQuery(id+"F1.wireOp",EDGE,"E71.56.left"),sQuery(id+"F1.wireOp",EDGE,"E71.56.right"),sQuery(id+"F1.wireOp",EDGE,"E71.58.startCap"),sQuery(id+"F1.wireOp",EDGE,"E71.58.left"),sQuery(id+"F1.wireOp",EDGE,"E71.58.right"),sQuery(id+"F1.wireOp",EDGE,"E71.59.startCap"),sQuery(id+"F1.wireOp",EDGE,"E71.59.endCap"),sQuery(id+"F1.wireOp",EDGE,"E71.59.left"),sQuery(id+"F1.wireOp",EDGE,"E71.59.right"),sQuery(id+"F1.wireOp",EDGE,"E71.62.startCap"),sQuery(id+"F1.wireOp",EDGE,"E71.62.left"),sQuery(id+"F1.wireOp",EDGE,"E71.62.right"),sQuery(id+"F1.wireOp",EDGE,"E71.63.startCap"),sQuery(id+"F1.wireOp",EDGE,"E71.63.endCap"),sQuery(id+"F1.wireOp",EDGE,"E71.63.left"),sQuery(id+"F1.wireOp",EDGE,"E71.63.right"),sQuery(id+"F1.wireOp",EDGE,"E71.64.startCap"),sQuery(id+"F1.wireOp",EDGE,"E71.64.endCap"),sQuery(id+"F1.wireOp",EDGE,"E71.64.left"),sQuery(id+"F1.wireOp",EDGE,"E71.64.right"),sQuery(id+"F1.wireOp",EDGE,"E71.65.startCap"),sQuery(id+"F1.wireOp",EDGE,"E71.65.endCap"),sQuery(id+"F1.wireOp",EDGE,"E71.65.left"),sQuery(id+"F1.wireOp",EDGE,"E71.65.right")])]});
            var Q38;
            Q38=makeQuery(id+"F5.opExtrude","SWEPT_BODY",BODY,{"disambiguationData":[OSD([sQuery(id+"F1.wireOp",EDGE,"E71.3.startCap"),sQuery(id+"F1.wireOp",EDGE,"E71.3.endCap"),sQuery(id+"F1.wireOp",EDGE,"E71.3.left"),sQuery(id+"F1.wireOp",EDGE,"E71.3.right")])]});
            var Q39;
            Q39=makeQuery(id+"F5.opExtrude","SWEPT_BODY",BODY,{"disambiguationData":[OSD([sQuery(id+"F1.wireOp",EDGE,"E71.8.endCap"),sQuery(id+"F1.wireOp",EDGE,"E71.8.left"),sQuery(id+"F1.wireOp",EDGE,"E71.8.right"),sQuery(id+"F1.wireOp",EDGE,"E71.31.startCap"),sQuery(id+"F1.wireOp",EDGE,"E71.31.left"),sQuery(id+"F1.wireOp",EDGE,"E71.31.right"),sQuery(id+"F1.wireOp",EDGE,"E71.43.startCap"),sQuery(id+"F1.wireOp",EDGE,"E71.43.endCap"),sQuery(id+"F1.wireOp",EDGE,"E71.43.left"),sQuery(id+"F1.wireOp",EDGE,"E71.43.right")])]});
            var Q40;
            Q40=makeQuery(id+"F5.opExtrude","SWEPT_BODY",BODY,{"disambiguationData":[OSD([sQuery(id+"F1.wireOp",EDGE,"E71.13.startCap"),sQuery(id+"F1.wireOp",EDGE,"E71.13.endCap"),sQuery(id+"F1.wireOp",EDGE,"E71.13.left"),sQuery(id+"F1.wireOp",EDGE,"E71.13.right")])]});
            var Q41;
            Q41=makeQuery(id+"F5.opExtrude","SWEPT_BODY",BODY,{"disambiguationData":[OSD([sQuery(id+"F1.wireOp",EDGE,"E71.17.startCap"),sQuery(id+"F1.wireOp",EDGE,"E71.17.left"),sQuery(id+"F1.wireOp",EDGE,"E71.17.right"),sQuery(id+"F1.wireOp",EDGE,"E71.18.startCap"),sQuery(id+"F1.wireOp",EDGE,"E71.18.left"),sQuery(id+"F1.wireOp",EDGE,"E71.18.right"),sQuery(id+"F1.wireOp",EDGE,"E71.25.startCap"),sQuery(id+"F1.wireOp",EDGE,"E71.25.left"),sQuery(id+"F1.wireOp",EDGE,"E71.25.right"),sQuery(id+"F1.wireOp",EDGE,"E71.34.left"),sQuery(id+"F1.wireOp",EDGE,"E71.34.right"),sQuery(id+"F1.wireOp",EDGE,"E71.41.startCap"),sQuery(id+"F1.wireOp",EDGE,"E71.41.endCap"),sQuery(id+"F1.wireOp",EDGE,"E71.41.left"),sQuery(id+"F1.wireOp",EDGE,"E71.41.right"),sQuery(id+"F1.wireOp",EDGE,"E71.45.startCap"),sQuery(id+"F1.wireOp",EDGE,"E71.45.endCap"),sQuery(id+"F1.wireOp",EDGE,"E71.45.left"),sQuery(id+"F1.wireOp",EDGE,"E71.45.right")])]});
            var Q42;
            Q42=makeQuery(id+"F5.opExtrude","SWEPT_BODY",BODY,{"disambiguationData":[OSD([sQuery(id+"F1.wireOp",EDGE,"E71.20.startCap"),sQuery(id+"F1.wireOp",EDGE,"E71.20.endCap"),sQuery(id+"F1.wireOp",EDGE,"E71.20.left"),sQuery(id+"F1.wireOp",EDGE,"E71.20.right")])]});
            var Q43;
            Q43=makeQuery(id+"F5.opExtrude","SWEPT_BODY",BODY,{"disambiguationData":[OSD([sQuery(id+"F1.wireOp",EDGE,"E71.22.startCap"),sQuery(id+"F1.wireOp",EDGE,"E71.22.endCap"),sQuery(id+"F1.wireOp",EDGE,"E71.22.left"),sQuery(id+"F1.wireOp",EDGE,"E71.22.right")])]});
            var Q44;
            Q44=makeQuery(id+"F5.opExtrude","SWEPT_BODY",BODY,{"disambiguationData":[OSD([sQuery(id+"F1.wireOp",EDGE,"E71.28.startCap"),sQuery(id+"F1.wireOp",EDGE,"E71.28.endCap"),sQuery(id+"F1.wireOp",EDGE,"E71.28.left"),sQuery(id+"F1.wireOp",EDGE,"E71.28.right")])]});
            var Q45;
            Q45=makeQuery(id+"F5.opExtrude","SWEPT_BODY",BODY,{"disambiguationData":[OSD([sQuery(id+"F1.wireOp",EDGE,"E71.29.startCap"),sQuery(id+"F1.wireOp",EDGE,"E71.29.endCap"),sQuery(id+"F1.wireOp",EDGE,"E71.29.left"),sQuery(id+"F1.wireOp",EDGE,"E71.29.right")])]});
            var Q46;
            Q46=makeQuery(id+"F5.opExtrude","SWEPT_BODY",BODY,{"disambiguationData":[OSD([sQuery(id+"F1.wireOp",EDGE,"E71.40.startCap"),sQuery(id+"F1.wireOp",EDGE,"E71.40.endCap"),sQuery(id+"F1.wireOp",EDGE,"E71.40.left"),sQuery(id+"F1.wireOp",EDGE,"E71.40.right")])]});
            var Q47;
            Q47=makeQuery(id+"F5.opExtrude","SWEPT_BODY",BODY,{"disambiguationData":[OSD([sQuery(id+"F1.wireOp",EDGE,"E71.44.startCap"),sQuery(id+"F1.wireOp",EDGE,"E71.44.endCap"),sQuery(id+"F1.wireOp",EDGE,"E71.44.left"),sQuery(id+"F1.wireOp",EDGE,"E71.44.right")])]});
            hole(context, id + "F7", {"style" : HoleStyle.SIMPLE, "endStyle" : HoleEndStyle.THROUGH, "holeDiameter" : 1 * mm, "majorDiameter" : 5 * mm, "isTappedThrough" : true, "tappedDepth" : 12 * mm, "tapClearance" : 3, "locations" : qUnion([Q0, Q1, Q2, Q3, Q4, Q5, Q6, Q7, Q8, Q9, Q10, Q11, Q12, Q13, Q14, Q15, Q16, Q17, Q18, Q19, Q20, Q21, Q22, Q23, Q24, Q25, Q26, Q27, Q28, Q29, Q30, Q31, Q32, Q33, Q34, Q35]), "scope" : qUnion([Q36, Q37, Q38, Q39, Q40, Q41, Q42, Q43, Q44, Q45, Q46, Q47])});
        }
        {
            var Q0;
            Q0=sQuery(id+"F2.wireOp",VERTEX,"E132");
            var Q1;
            Q1=sQuery(id+"F2.wireOp",VERTEX,"E148");
            var Q2;
            Q2=sQuery(id+"F2.wireOp",VERTEX,"E147");
            var Q3;
            Q3=sQuery(id+"F2.wireOp",VERTEX,"E145");
            var Q4;
            Q4=sQuery(id+"F2.wireOp",VERTEX,"E134");
            var Q5;
            Q5=sQuery(id+"F2.wireOp",VERTEX,"E135");
            var Q6;
            Q6=sQuery(id+"F2.wireOp",VERTEX,"E133");
            var Q7;
            Q7=sQuery(id+"F2.wireOp",VERTEX,"E139");
            var Q8;
            Q8=sQuery(id+"F2.wireOp",VERTEX,"E123");
            var Q9;
            Q9=sQuery(id+"F2.wireOp",VERTEX,"E144");
            var Q10;
            Q10=sQuery(id+"F2.wireOp",VERTEX,"E126");
            var Q11;
            Q11=sQuery(id+"F2.wireOp",VERTEX,"E127");
            var Q12;
            Q12=sQuery(id+"F2.wireOp",VERTEX,"E124");
            var Q13;
            Q13=sQuery(id+"F2.wireOp",VERTEX,"E140");
            var Q14;
            Q14=sQuery(id+"F2.wireOp",VERTEX,"E138");
            var Q15;
            Q15=sQuery(id+"F2.wireOp",VERTEX,"E137");
            var Q16;
            Q16=sQuery(id+"F2.wireOp",VERTEX,"E131");
            var Q17;
            Q17=sQuery(id+"F2.wireOp",VERTEX,"E146");
            var Q18;
            Q18=sQuery(id+"F2.wireOp",VERTEX,"E125");
            var Q19;
            Q19=sQuery(id+"F2.wireOp",VERTEX,"E149");
            var Q20;
            Q20=sQuery(id+"F2.wireOp",VERTEX,"E136");
            var Q21;
            Q21=makeQuery(id+"F3.opExtrude","SWEPT_BODY",BODY,{"disambiguationData":[OSD([sQuery(id+"F0.wireOp",EDGE,"E0.bottom"),sQuery(id+"F0.wireOp",EDGE,"E0.top"),sQuery(id+"F0.wireOp",EDGE,"E0.left"),sQuery(id+"F0.wireOp",EDGE,"E0.right")])]});
            var Q22;
            Q22=makeQuery(id+"F5.opExtrude","SWEPT_BODY",BODY,{"disambiguationData":[OSD([sQuery(id+"F1.wireOp",EDGE,"E71.1.left"),sQuery(id+"F1.wireOp",EDGE,"E71.1.right"),sQuery(id+"F1.wireOp",EDGE,"E71.4.left"),sQuery(id+"F1.wireOp",EDGE,"E71.4.right"),sQuery(id+"F1.wireOp",EDGE,"E71.5.left"),sQuery(id+"F1.wireOp",EDGE,"E71.5.right"),sQuery(id+"F1.wireOp",EDGE,"E71.6.startCap"),sQuery(id+"F1.wireOp",EDGE,"E71.6.left"),sQuery(id+"F1.wireOp",EDGE,"E71.6.right"),sQuery(id+"F1.wireOp",EDGE,"E71.7.left"),sQuery(id+"F1.wireOp",EDGE,"E71.7.right"),sQuery(id+"F1.wireOp",EDGE,"E71.9.startCap"),sQuery(id+"F1.wireOp",EDGE,"E71.9.left"),sQuery(id+"F1.wireOp",EDGE,"E71.9.right"),sQuery(id+"F1.wireOp",EDGE,"E71.10.left"),sQuery(id+"F1.wireOp",EDGE,"E71.10.right"),sQuery(id+"F1.wireOp",EDGE,"E71.11.left"),sQuery(id+"F1.wireOp",EDGE,"E71.11.right"),sQuery(id+"F1.wireOp",EDGE,"E71.12.startCap"),sQuery(id+"F1.wireOp",EDGE,"E71.12.endCap"),sQuery(id+"F1.wireOp",EDGE,"E71.12.left"),sQuery(id+"F1.wireOp",EDGE,"E71.12.right"),sQuery(id+"F1.wireOp",EDGE,"E71.16.startCap"),sQuery(id+"F1.wireOp",EDGE,"E71.16.left"),sQuery(id+"F1.wireOp",EDGE,"E71.16.right"),sQuery(id+"F1.wireOp",EDGE,"E71.19.startCap"),sQuery(id+"F1.wireOp",EDGE,"E71.19.endCap"),sQuery(id+"F1.wireOp",EDGE,"E71.19.left"),sQuery(id+"F1.wireOp",EDGE,"E71.19.right"),sQuery(id+"F1.wireOp",EDGE,"E71.21.endCap"),sQuery(id+"F1.wireOp",EDGE,"E71.21.left"),sQuery(id+"F1.wireOp",EDGE,"E71.21.right"),sQuery(id+"F1.wireOp",EDGE,"E71.26.startCap"),sQuery(id+"F1.wireOp",EDGE,"E71.26.left"),sQuery(id+"F1.wireOp",EDGE,"E71.26.right"),sQuery(id+"F1.wireOp",EDGE,"E71.30.startCap"),sQuery(id+"F1.wireOp",EDGE,"E71.30.left"),sQuery(id+"F1.wireOp",EDGE,"E71.30.right"),sQuery(id+"F1.wireOp",EDGE,"E71.32.left"),sQuery(id+"F1.wireOp",EDGE,"E71.32.right"),sQuery(id+"F1.wireOp",EDGE,"E71.33.endCap"),sQuery(id+"F1.wireOp",EDGE,"E71.33.left"),sQuery(id+"F1.wireOp",EDGE,"E71.33.right"),sQuery(id+"F1.wireOp",EDGE,"E71.37.left"),sQuery(id+"F1.wireOp",EDGE,"E71.37.right"),sQuery(id+"F1.wireOp",EDGE,"E71.38.startCap"),sQuery(id+"F1.wireOp",EDGE,"E71.38.endCap"),sQuery(id+"F1.wireOp",EDGE,"E71.38.left"),sQuery(id+"F1.wireOp",EDGE,"E71.38.right"),sQuery(id+"F1.wireOp",EDGE,"E71.46.startCap"),sQuery(id+"F1.wireOp",EDGE,"E71.46.left"),sQuery(id+"F1.wireOp",EDGE,"E71.46.right"),sQuery(id+"F1.wireOp",EDGE,"E71.47.left"),sQuery(id+"F1.wireOp",EDGE,"E71.47.right"),sQuery(id+"F1.wireOp",EDGE,"E71.49.left"),sQuery(id+"F1.wireOp",EDGE,"E71.49.right"),sQuery(id+"F1.wireOp",EDGE,"E71.51.startCap"),sQuery(id+"F1.wireOp",EDGE,"E71.51.endCap"),sQuery(id+"F1.wireOp",EDGE,"E71.51.left"),sQuery(id+"F1.wireOp",EDGE,"E71.51.right"),sQuery(id+"F1.wireOp",EDGE,"E71.53.startCap"),sQuery(id+"F1.wireOp",EDGE,"E71.53.endCap"),sQuery(id+"F1.wireOp",EDGE,"E71.53.left"),sQuery(id+"F1.wireOp",EDGE,"E71.53.right"),sQuery(id+"F1.wireOp",EDGE,"E71.54.startCap"),sQuery(id+"F1.wireOp",EDGE,"E71.54.endCap"),sQuery(id+"F1.wireOp",EDGE,"E71.54.left"),sQuery(id+"F1.wireOp",EDGE,"E71.54.right"),sQuery(id+"F1.wireOp",EDGE,"E71.55.endCap"),sQuery(id+"F1.wireOp",EDGE,"E71.55.left"),sQuery(id+"F1.wireOp",EDGE,"E71.55.right"),sQuery(id+"F1.wireOp",EDGE,"E71.56.endCap"),sQuery(id+"F1.wireOp",EDGE,"E71.56.left"),sQuery(id+"F1.wireOp",EDGE,"E71.56.right"),sQuery(id+"F1.wireOp",EDGE,"E71.58.startCap"),sQuery(id+"F1.wireOp",EDGE,"E71.58.left"),sQuery(id+"F1.wireOp",EDGE,"E71.58.right"),sQuery(id+"F1.wireOp",EDGE,"E71.59.startCap"),sQuery(id+"F1.wireOp",EDGE,"E71.59.endCap"),sQuery(id+"F1.wireOp",EDGE,"E71.59.left"),sQuery(id+"F1.wireOp",EDGE,"E71.59.right"),sQuery(id+"F1.wireOp",EDGE,"E71.62.startCap"),sQuery(id+"F1.wireOp",EDGE,"E71.62.left"),sQuery(id+"F1.wireOp",EDGE,"E71.62.right"),sQuery(id+"F1.wireOp",EDGE,"E71.63.startCap"),sQuery(id+"F1.wireOp",EDGE,"E71.63.endCap"),sQuery(id+"F1.wireOp",EDGE,"E71.63.left"),sQuery(id+"F1.wireOp",EDGE,"E71.63.right"),sQuery(id+"F1.wireOp",EDGE,"E71.64.startCap"),sQuery(id+"F1.wireOp",EDGE,"E71.64.endCap"),sQuery(id+"F1.wireOp",EDGE,"E71.64.left"),sQuery(id+"F1.wireOp",EDGE,"E71.64.right"),sQuery(id+"F1.wireOp",EDGE,"E71.65.startCap"),sQuery(id+"F1.wireOp",EDGE,"E71.65.endCap"),sQuery(id+"F1.wireOp",EDGE,"E71.65.left"),sQuery(id+"F1.wireOp",EDGE,"E71.65.right")])]});
            var Q23;
            Q23=makeQuery(id+"F5.opExtrude","SWEPT_BODY",BODY,{"disambiguationData":[OSD([sQuery(id+"F1.wireOp",EDGE,"E71.8.endCap"),sQuery(id+"F1.wireOp",EDGE,"E71.8.left"),sQuery(id+"F1.wireOp",EDGE,"E71.8.right"),sQuery(id+"F1.wireOp",EDGE,"E71.31.startCap"),sQuery(id+"F1.wireOp",EDGE,"E71.31.left"),sQuery(id+"F1.wireOp",EDGE,"E71.31.right"),sQuery(id+"F1.wireOp",EDGE,"E71.43.startCap"),sQuery(id+"F1.wireOp",EDGE,"E71.43.endCap"),sQuery(id+"F1.wireOp",EDGE,"E71.43.left"),sQuery(id+"F1.wireOp",EDGE,"E71.43.right")])]});
            var Q24;
            Q24=makeQuery(id+"F5.opExtrude","SWEPT_BODY",BODY,{"disambiguationData":[OSD([sQuery(id+"F1.wireOp",EDGE,"E71.17.startCap"),sQuery(id+"F1.wireOp",EDGE,"E71.17.left"),sQuery(id+"F1.wireOp",EDGE,"E71.17.right"),sQuery(id+"F1.wireOp",EDGE,"E71.18.startCap"),sQuery(id+"F1.wireOp",EDGE,"E71.18.left"),sQuery(id+"F1.wireOp",EDGE,"E71.18.right"),sQuery(id+"F1.wireOp",EDGE,"E71.25.startCap"),sQuery(id+"F1.wireOp",EDGE,"E71.25.left"),sQuery(id+"F1.wireOp",EDGE,"E71.25.right"),sQuery(id+"F1.wireOp",EDGE,"E71.34.left"),sQuery(id+"F1.wireOp",EDGE,"E71.34.right"),sQuery(id+"F1.wireOp",EDGE,"E71.41.startCap"),sQuery(id+"F1.wireOp",EDGE,"E71.41.endCap"),sQuery(id+"F1.wireOp",EDGE,"E71.41.left"),sQuery(id+"F1.wireOp",EDGE,"E71.41.right"),sQuery(id+"F1.wireOp",EDGE,"E71.45.startCap"),sQuery(id+"F1.wireOp",EDGE,"E71.45.endCap"),sQuery(id+"F1.wireOp",EDGE,"E71.45.left"),sQuery(id+"F1.wireOp",EDGE,"E71.45.right")])]});
            hole(context, id + "F8", {"style" : HoleStyle.SIMPLE, "endStyle" : HoleEndStyle.THROUGH, "holeDiameter" : 1 * mm, "majorDiameter" : 5 * mm, "isTappedThrough" : true, "tappedDepth" : 12 * mm, "tapClearance" : 3, "locations" : qUnion([Q0, Q1, Q2, Q3, Q4, Q5, Q6, Q7, Q8, Q9, Q10, Q11, Q12, Q13, Q14, Q15, Q16, Q17, Q18, Q19, Q20]), "scope" : qUnion([Q21, Q22, Q23, Q24])});
        }
    });
